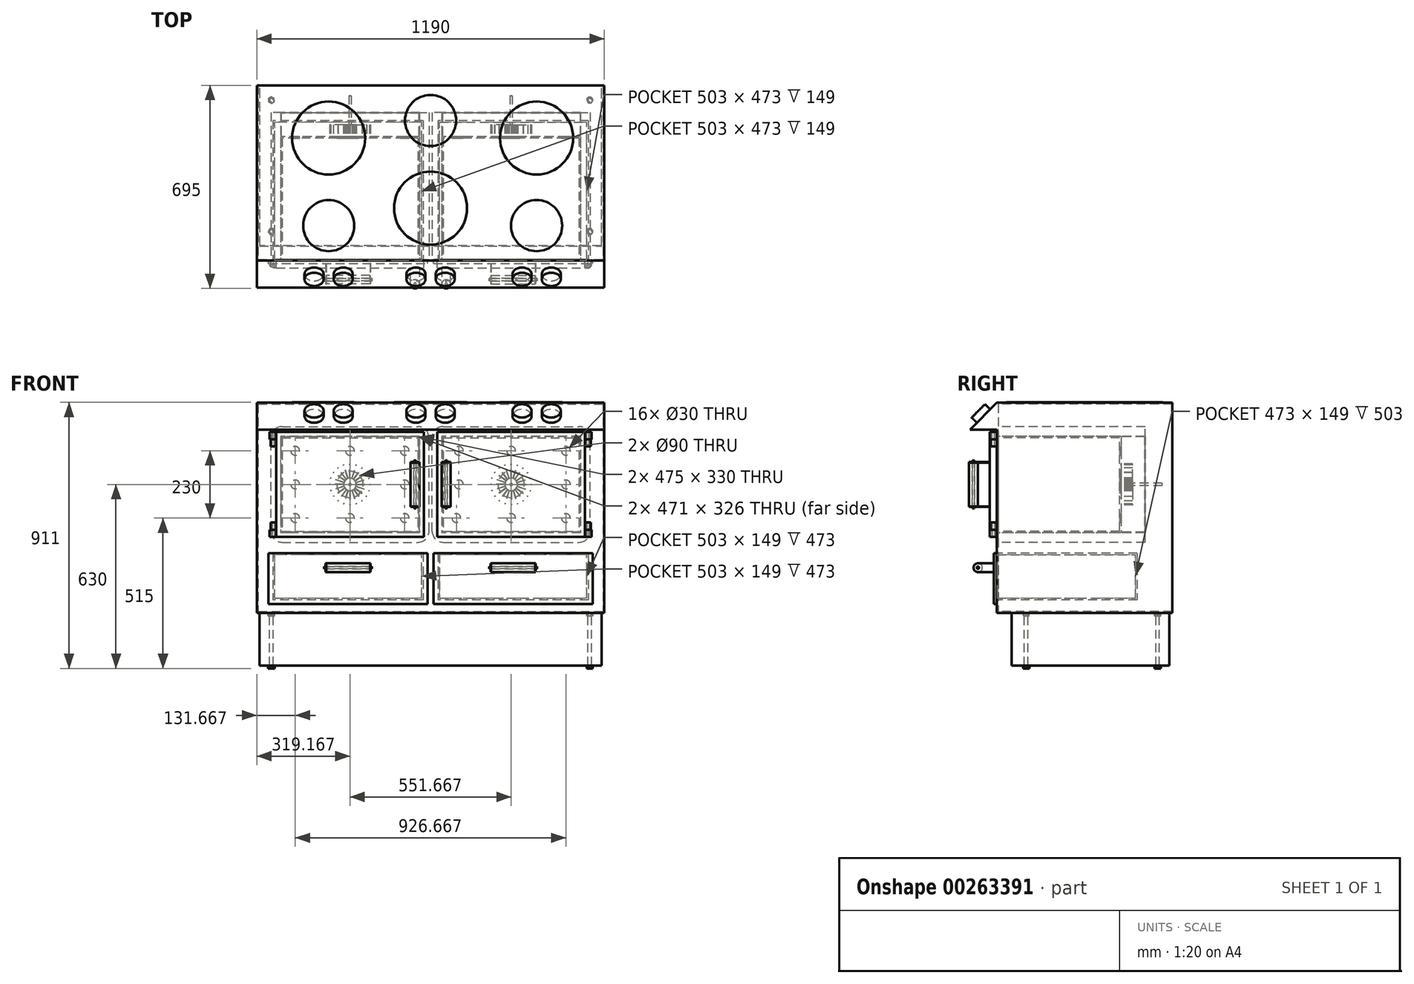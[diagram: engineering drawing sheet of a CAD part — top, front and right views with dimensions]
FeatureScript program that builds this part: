
annotation { "Feature Type Name" : "Feature", "Feature Type Description" : "" }
export const myFeature = defineFeature(function(context is Context, id is Id, definition is map)
    precondition{}
    {
        {
            assignVariable(context, id + "F0", {"name" : "Height", "anyValue" : 910});
        }
        {
            assignVariable(context, id + "F1", {"name" : "Thickness", "anyValue" : 5});
        }
        {
            assignVariable(context, id + "F2", {"name" : "OvenDepth", "anyValue" : 420});
        }
        {
            assignVariable(context, id + "F3", {"name" : "ToeHeight", "anyValue" : 190});
        }
        {
            var Q0;
            Q0=qCreatedBy(makeId("Top.planeOp"),FACE);
            cPlane(context, id + "F4", {"entities" : qUnion([Q0]), "cplaneType" : CPlaneType.OFFSET, "offset" : (getVariable(context, 'ToeHeight')) * mm, "width" : 150 * mm, "height" : 150 * mm});
        }
        {
            var Q0;
            Q0=qCreatedBy(id+"F4.planeOp",FACE);
            var sketch = newSketch(context, id + "F5", { "sketchPlane" : qUnion([Q0])});
            skLineSegment(sketch, "E0.bottom", {"start": v(0, 0) * mm, "end": v(1190, 0) * mm});
            skLineSegment(sketch, "E0.top", {"start": v(0, -600) * mm, "end": v(1190, -600) * mm});
            skLineSegment(sketch, "E0.left", {"start": v(0, 0) * mm, "end": v(0, -600) * mm});
            skLineSegment(sketch, "E0.right", {"start": v(1190, 0) * mm, "end": v(1190, -600) * mm});
            skSolve(sketch);
        }
        {
            var Q0;
            Q0 = qSketchRegion(id + "F5", true);
            extrude(context, id + "F6", {"entities" : qUnion([Q0]), "depth" : (getVariable(context, 'Height') - getVariable(context, 'ToeHeight')) * mm});
        }
        {
            var Q0;
            Q0=makeQuery(id+"F6.opExtrude","SWEPT_FACE",FACE,{"disambiguationData":[OSD([sQuery(id+"F5.wireOp",EDGE,"E0.bottom")])]});
            var Q1;
            Q1=makeQuery(id+"F6.opExtrude","SWEPT_BODY",BODY,{"disambiguationData":[OSD([sQuery(id+"F5.wireOp",EDGE,"E0.bottom"),sQuery(id+"F5.wireOp",EDGE,"E0.top"),sQuery(id+"F5.wireOp",EDGE,"E0.left"),sQuery(id+"F5.wireOp",EDGE,"E0.right")])]});
            shell(context, id + "F7", {"entities" : qUnion([Q0]), "parts" : qUnion([Q1]), "thickness" : (getVariable(context, 'Thickness')) * mm});
        }
        {
            var Q0;
            Q0=makeQuery(id+"F6.opExtrude","SWEPT_FACE",FACE,{"disambiguationData":[OSD([sQuery(id+"F5.wireOp",EDGE,"E0.top")])]});
            var sketch = newSketch(context, id + "F8", { "sketchPlane" : qUnion([Q0])});
            skLineSegment(sketch, "E1.bottom", {"start": v(638.33, 790) * mm, "end": v(1103.33, 790) * mm});
            skLineSegment(sketch, "E1.top", {"start": v(638.33, 470) * mm, "end": v(1103.33, 470) * mm});
            skLineSegment(sketch, "E1.left", {"start": v(638.33, 790) * mm, "end": v(638.33, 470) * mm});
            skLineSegment(sketch, "E1.right", {"start": v(1103.33, 790) * mm, "end": v(1103.33, 470) * mm});
            skLineSegment(sketch, "E2.bottom", {"start": v(86.67, 790) * mm, "end": v(551.67, 790) * mm});
            skLineSegment(sketch, "E2.top", {"start": v(86.67, 470) * mm, "end": v(551.67, 470) * mm});
            skLineSegment(sketch, "E2.left", {"start": v(86.67, 790) * mm, "end": v(86.67, 470) * mm});
            skLineSegment(sketch, "E2.right", {"start": v(551.67, 790) * mm, "end": v(551.67, 470) * mm});
            skLineSegment(sketch, "E3", {"start": v(0, 550) * mm, "end": v(86.67, 550) * mm, "construction": true});
            skLineSegment(sketch, "E4", {"start": v(551.67, 550) * mm, "end": v(638.33, 550) * mm, "construction": true});
            skLineSegment(sketch, "E5", {"start": v(1103.33, 550) * mm, "end": v(1190, 550) * mm, "construction": true});
            skSolve(sketch);
        }
        {
            var Q0;
            Q0 = qSketchRegion(id + "F8", true);
            extrude(context, id + "F9", {"entities" : qUnion([Q0]), "operationType" : NewBodyOperationType.REMOVE, "oppositeDirection" : true, "depth" : 25 * mm});
        }
        {
            var Q0;
            Q0=makeQuery(id+"F7.opShell","OFFSET_FACE",FACE,{"disambiguationData":[OSD([sQuery(id+"F5.wireOp",EDGE,"E0.top")])]});
            var sketch = newSketch(context, id + "F10", { "sketchPlane" : qUnion([Q0])});
            skLineSegment(sketch, "E6.0", {"start": v(-1103.33, 790) * mm, "end": v(-638.33, 790) * mm});
            skLineSegment(sketch, "E7.0", {"start": v(-1103.33, 470) * mm, "end": v(-1103.33, 790) * mm});
            skLineSegment(sketch, "E8.0", {"start": v(-1103.33, 470) * mm, "end": v(-638.33, 470) * mm});
            skLineSegment(sketch, "E9.0", {"start": v(-638.33, 470) * mm, "end": v(-638.33, 790) * mm});
            skLineSegment(sketch, "E10.0", {"start": v(-551.67, 470) * mm, "end": v(-551.67, 790) * mm});
            skLineSegment(sketch, "E11.0", {"start": v(-551.67, 790) * mm, "end": v(-86.67, 790) * mm});
            skLineSegment(sketch, "E12.0", {"start": v(-86.67, 470) * mm, "end": v(-86.67, 790) * mm});
            skLineSegment(sketch, "E13.0", {"start": v(-551.67, 470) * mm, "end": v(-86.67, 470) * mm});
            skLineSegment(sketch, "E14.bottom", {"start": v(-1108.33, 795) * mm, "end": v(-633.33, 795) * mm});
            skLineSegment(sketch, "E14.top", {"start": v(-1108.33, 465) * mm, "end": v(-633.33, 465) * mm});
            skLineSegment(sketch, "E14.left", {"start": v(-1108.33, 795) * mm, "end": v(-1108.33, 465) * mm});
            skLineSegment(sketch, "E14.right", {"start": v(-633.33, 795) * mm, "end": v(-633.33, 465) * mm});
            skLineSegment(sketch, "E15.bottom", {"start": v(-556.67, 795) * mm, "end": v(-81.67, 795) * mm});
            skLineSegment(sketch, "E15.top", {"start": v(-556.67, 465) * mm, "end": v(-81.67, 465) * mm});
            skLineSegment(sketch, "E15.left", {"start": v(-556.67, 795) * mm, "end": v(-556.67, 465) * mm});
            skLineSegment(sketch, "E15.right", {"start": v(-81.67, 795) * mm, "end": v(-81.67, 465) * mm});
            skSolve(sketch);
        }
        {
            var Q0;
            Q0 = qSketchRegion(id + "F10", true);
            extrude(context, id + "F11", {"entities" : qUnion([Q0]), "operationType" : NewBodyOperationType.ADD, "depth" : (getVariable(context, 'OvenDepth') - getVariable(context, 'Thickness')) * mm});
        }
        {
            var Q0;
            Q0=makeQuery(id+"F11.opExtrude","CAP_FACE",FACE,{"disambiguationData":[OSD([sQuery(id+"F10.wireOp",EDGE,"E6.0"),sQuery(id+"F10.wireOp",EDGE,"E7.0"),sQuery(id+"F10.wireOp",EDGE,"E8.0"),sQuery(id+"F10.wireOp",EDGE,"E9.0"),sQuery(id+"F10.wireOp",EDGE,"E14.bottom"),sQuery(id+"F10.wireOp",EDGE,"E14.top"),sQuery(id+"F10.wireOp",EDGE,"E14.left"),sQuery(id+"F10.wireOp",EDGE,"E14.right")])],"isStart":false});
            var sketch = newSketch(context, id + "F12", { "sketchPlane" : qUnion([Q0])});
            skLineSegment(sketch, "E16.bottom", {"start": v(-1108.33, 795) * mm, "end": v(-633.33, 795) * mm});
            skLineSegment(sketch, "E16.top", {"start": v(-1108.33, 465) * mm, "end": v(-633.33, 465) * mm});
            skLineSegment(sketch, "E16.left", {"start": v(-1108.33, 795) * mm, "end": v(-1108.33, 465) * mm});
            skLineSegment(sketch, "E16.right", {"start": v(-633.33, 795) * mm, "end": v(-633.33, 465) * mm});
            skLineSegment(sketch, "E17.bottom", {"start": v(-556.67, 795) * mm, "end": v(-81.67, 795) * mm});
            skLineSegment(sketch, "E17.top", {"start": v(-556.67, 465) * mm, "end": v(-81.67, 465) * mm});
            skLineSegment(sketch, "E17.left", {"start": v(-556.67, 795) * mm, "end": v(-556.67, 465) * mm});
            skLineSegment(sketch, "E17.right", {"start": v(-81.67, 795) * mm, "end": v(-81.67, 465) * mm});
            skSolve(sketch);
        }
        {
            var Q0;
            Q0 = qSketchRegion(id + "F12", true);
            extrude(context, id + "F13", {"entities" : qUnion([Q0]), "operationType" : NewBodyOperationType.ADD, "depth" : (getVariable(context, 'Thickness')) * mm});
        }
        {
            var Q0;
            Q0=makeQuery(id+"F6.opExtrude","SWEPT_FACE",FACE,{"disambiguationData":[OSD([sQuery(id+"F5.wireOp",EDGE,"E0.top")])]});
            var sketch = newSketch(context, id + "F14", { "sketchPlane" : qUnion([Q0])});
            skLineSegment(sketch, "E18.bottom", {"start": v(60, 390) * mm, "end": v(565, 390) * mm});
            skLineSegment(sketch, "E18.top", {"start": v(60, 240) * mm, "end": v(565, 240) * mm});
            skLineSegment(sketch, "E18.left", {"start": v(60, 390) * mm, "end": v(60, 240) * mm});
            skLineSegment(sketch, "E18.right", {"start": v(565, 390) * mm, "end": v(565, 240) * mm});
            skLineSegment(sketch, "E19.bottom", {"start": v(625, 390) * mm, "end": v(1130, 390) * mm});
            skLineSegment(sketch, "E19.top", {"start": v(625, 240) * mm, "end": v(1130, 240) * mm});
            skLineSegment(sketch, "E19.left", {"start": v(625, 390) * mm, "end": v(625, 240) * mm});
            skLineSegment(sketch, "E19.right", {"start": v(1130, 390) * mm, "end": v(1130, 240) * mm});
            skLineSegment(sketch, "E20", {"start": v(0, 306.12) * mm, "end": v(60, 306.12) * mm, "construction": true});
            skLineSegment(sketch, "E21", {"start": v(565, 306.12) * mm, "end": v(625, 306.12) * mm, "construction": true});
            skLineSegment(sketch, "E22", {"start": v(1130, 306.12) * mm, "end": v(1190, 306.12) * mm, "construction": true});
            skPoint(sketch, "E22.startSnap0", {"position": v(1130, 315) * mm});
            skLineSegment(sketch, "E23", {"start": v(293.85, 470) * mm, "end": v(293.85, 390) * mm, "construction": true});
            skLineSegment(sketch, "E24", {"start": v(312.5, 240) * mm, "end": v(312.5, 160) * mm, "construction": true});
            skSolve(sketch);
        }
        {
            var Q0;
            Q0 = qSketchRegion(id + "F14", true);
            extrude(context, id + "F15", {"entities" : qUnion([Q0]), "operationType" : NewBodyOperationType.REMOVE, "oppositeDirection" : true, "depth" : 25 * mm});
        }
        {
            var Q0;
            Q0=makeQuery(id+"F7.opShell","OFFSET_FACE",FACE,{"disambiguationData":[OSD([sQuery(id+"F5.wireOp",EDGE,"E0.top")])]});
            var sketch = newSketch(context, id + "F16", { "sketchPlane" : qUnion([Q0])});
            skLineSegment(sketch, "E25.0", {"start": v(-1130, 240) * mm, "end": v(-625, 240) * mm});
            skLineSegment(sketch, "E26.0", {"start": v(-1130, 390) * mm, "end": v(-625, 390) * mm});
            skLineSegment(sketch, "E27.0", {"start": v(-1130, 240) * mm, "end": v(-1130, 390) * mm});
            skLineSegment(sketch, "E28.0", {"start": v(-625, 240) * mm, "end": v(-625, 390) * mm});
            skLineSegment(sketch, "E29.0", {"start": v(-565, 240) * mm, "end": v(-565, 390) * mm});
            skLineSegment(sketch, "E30.0", {"start": v(-565, 390) * mm, "end": v(-60, 390) * mm});
            skLineSegment(sketch, "E31.0", {"start": v(-60, 240) * mm, "end": v(-60, 390) * mm});
            skLineSegment(sketch, "E32.0", {"start": v(-565, 240) * mm, "end": v(-60, 240) * mm});
            skLineSegment(sketch, "E33.bottom", {"start": v(-1135, 395) * mm, "end": v(-620, 395) * mm});
            skLineSegment(sketch, "E33.top", {"start": v(-1135, 235) * mm, "end": v(-620, 235) * mm});
            skLineSegment(sketch, "E33.left", {"start": v(-1135, 395) * mm, "end": v(-1135, 235) * mm});
            skLineSegment(sketch, "E33.right", {"start": v(-620, 395) * mm, "end": v(-620, 235) * mm});
            skLineSegment(sketch, "E34.bottom", {"start": v(-570, 395) * mm, "end": v(-55, 395) * mm});
            skLineSegment(sketch, "E34.top", {"start": v(-570, 235) * mm, "end": v(-55, 235) * mm});
            skLineSegment(sketch, "E34.left", {"start": v(-570, 395) * mm, "end": v(-570, 235) * mm});
            skLineSegment(sketch, "E34.right", {"start": v(-55, 395) * mm, "end": v(-55, 235) * mm});
            skSolve(sketch);
        }
        {
            var Q0;
            Q0 = qSketchRegion(id + "F16", true);
            extrude(context, id + "F17", {"entities" : qUnion([Q0]), "operationType" : NewBodyOperationType.ADD, "depth" : (getVariable(context, 'OvenDepth') + 50) * mm});
        }
        {
            var Q0;
            Q0=makeQuery(id+"F17.opExtrude","CAP_FACE",FACE,{"disambiguationData":[OSD([sQuery(id+"F16.wireOp",EDGE,"E25.0"),sQuery(id+"F16.wireOp",EDGE,"E26.0"),sQuery(id+"F16.wireOp",EDGE,"E27.0"),sQuery(id+"F16.wireOp",EDGE,"E28.0"),sQuery(id+"F16.wireOp",EDGE,"E33.bottom"),sQuery(id+"F16.wireOp",EDGE,"E33.top"),sQuery(id+"F16.wireOp",EDGE,"E33.left"),sQuery(id+"F16.wireOp",EDGE,"E33.right")])],"isStart":false});
            var sketch = newSketch(context, id + "F18", { "sketchPlane" : qUnion([Q0])});
            skLineSegment(sketch, "E35.bottom", {"start": v(-1135, 395) * mm, "end": v(-620, 395) * mm});
            skLineSegment(sketch, "E35.top", {"start": v(-1135, 235) * mm, "end": v(-620, 235) * mm});
            skLineSegment(sketch, "E35.left", {"start": v(-1135, 395) * mm, "end": v(-1135, 235) * mm});
            skLineSegment(sketch, "E35.right", {"start": v(-620, 395) * mm, "end": v(-620, 235) * mm});
            skLineSegment(sketch, "E36.bottom", {"start": v(-570, 395) * mm, "end": v(-55, 395) * mm});
            skLineSegment(sketch, "E36.top", {"start": v(-570, 235) * mm, "end": v(-55, 235) * mm});
            skLineSegment(sketch, "E36.left", {"start": v(-570, 395) * mm, "end": v(-570, 235) * mm});
            skLineSegment(sketch, "E36.right", {"start": v(-55, 395) * mm, "end": v(-55, 235) * mm});
            skSolve(sketch);
        }
        {
            var Q0;
            Q0 = qSketchRegion(id + "F18", true);
            extrude(context, id + "F19", {"entities" : qUnion([Q0]), "operationType" : NewBodyOperationType.ADD, "depth" : (getVariable(context, 'Thickness')) * mm});
        }
        {
            var Q0;
            Q0=makeQuery(id+"F6.opExtrude","CAP_FACE",FACE,{"disambiguationData":[OSD([sQuery(id+"F5.wireOp",EDGE,"E0.bottom"),sQuery(id+"F5.wireOp",EDGE,"E0.top"),sQuery(id+"F5.wireOp",EDGE,"E0.left"),sQuery(id+"F5.wireOp",EDGE,"E0.right")])],"isStart":true});
            var sketch = newSketch(context, id + "F20", { "sketchPlane" : qUnion([Q0])});
            skCircle(sketch, "E37.cCircle", {"center": v(50, 500) * mm, "radius": 9.5 * mm, "construction": true});
            skLineSegment(sketch, "E37.0", {"start": v(55.48, 490.5) * mm, "end": v(44.52, 490.5) * mm});
            skLineSegment(sketch, "E37.1", {"start": v(44.52, 490.5) * mm, "end": v(39.03, 500) * mm});
            skLineSegment(sketch, "E37.2", {"start": v(39.03, 500) * mm, "end": v(44.52, 509.5) * mm});
            skLineSegment(sketch, "E37.3", {"start": v(44.52, 509.5) * mm, "end": v(55.48, 509.5) * mm});
            skLineSegment(sketch, "E37.4", {"start": v(55.48, 509.5) * mm, "end": v(60.97, 500) * mm});
            skLineSegment(sketch, "E37.5", {"start": v(60.97, 500) * mm, "end": v(55.48, 490.5) * mm});
            skPoint(sketch, "E37.0.midPoint", {"position": v(50, 490.5) * mm});
            skCircle(sketch, "E38.cCircle", {"center": v(1140, 500) * mm, "radius": 9.5 * mm, "construction": true});
            skLineSegment(sketch, "E38.0", {"start": v(1145.48, 490.5) * mm, "end": v(1134.52, 490.5) * mm});
            skLineSegment(sketch, "E38.1", {"start": v(1134.52, 490.5) * mm, "end": v(1129.03, 500) * mm});
            skLineSegment(sketch, "E38.2", {"start": v(1129.03, 500) * mm, "end": v(1134.52, 509.5) * mm});
            skLineSegment(sketch, "E38.3", {"start": v(1134.52, 509.5) * mm, "end": v(1145.48, 509.5) * mm});
            skLineSegment(sketch, "E38.4", {"start": v(1145.48, 509.5) * mm, "end": v(1150.97, 500) * mm});
            skLineSegment(sketch, "E38.5", {"start": v(1150.97, 500) * mm, "end": v(1145.48, 490.5) * mm});
            skPoint(sketch, "E38.0.midPoint", {"position": v(1140, 490.5) * mm});
            skCircle(sketch, "E39.cCircle", {"center": v(1140, 50) * mm, "radius": 9.5 * mm, "construction": true});
            skLineSegment(sketch, "E39.0", {"start": v(1150.97, 50) * mm, "end": v(1145.48, 40.5) * mm});
            skLineSegment(sketch, "E39.1", {"start": v(1145.48, 40.5) * mm, "end": v(1134.52, 40.5) * mm});
            skLineSegment(sketch, "E39.2", {"start": v(1134.52, 40.5) * mm, "end": v(1129.03, 50) * mm});
            skLineSegment(sketch, "E39.3", {"start": v(1129.03, 50) * mm, "end": v(1134.52, 59.5) * mm});
            skLineSegment(sketch, "E39.4", {"start": v(1134.52, 59.5) * mm, "end": v(1145.48, 59.5) * mm});
            skLineSegment(sketch, "E39.5", {"start": v(1145.48, 59.5) * mm, "end": v(1150.97, 50) * mm});
            skPoint(sketch, "E39.0.midPoint", {"position": v(1148.23, 45.25) * mm});
            skCircle(sketch, "E40.cCircle", {"center": v(50, 50) * mm, "radius": 9.5 * mm, "construction": true});
            skLineSegment(sketch, "E40.0", {"start": v(49, 39.08) * mm, "end": v(40.04, 45.4) * mm});
            skLineSegment(sketch, "E40.1", {"start": v(40.04, 45.4) * mm, "end": v(41.04, 56.33) * mm});
            skLineSegment(sketch, "E40.2", {"start": v(41.04, 56.33) * mm, "end": v(51, 60.92) * mm});
            skLineSegment(sketch, "E40.3", {"start": v(51, 60.92) * mm, "end": v(59.96, 54.6) * mm});
            skLineSegment(sketch, "E40.4", {"start": v(59.96, 54.6) * mm, "end": v(58.96, 43.67) * mm});
            skLineSegment(sketch, "E40.5", {"start": v(58.96, 43.67) * mm, "end": v(49, 39.08) * mm});
            skPoint(sketch, "E40.0.midPoint", {"position": v(44.52, 42.24) * mm});
            skCircle(sketch, "E41", {"center": v(50, 500) * mm, "radius": 6 * mm});
            skCircle(sketch, "E42", {"center": v(50, 50) * mm, "radius": 6 * mm});
            skCircle(sketch, "E43", {"center": v(1140, 50) * mm, "radius": 6 * mm});
            skCircle(sketch, "E44", {"center": v(1140, 500) * mm, "radius": 6 * mm});
            skSolve(sketch);
        }
        {
            var Q0;
            Q0 = qSketchRegion(id + "F20", true);
            extrude(context, id + "F21", {"entities" : qUnion([Q0]), "depth" : 10 * mm});
        }
        {
            var Q0;
            Q0=makeQuery(id+"F6.opExtrude","CAP_FACE",FACE,{"disambiguationData":[OSD([sQuery(id+"F5.wireOp",EDGE,"E0.bottom"),sQuery(id+"F5.wireOp",EDGE,"E0.top"),sQuery(id+"F5.wireOp",EDGE,"E0.left"),sQuery(id+"F5.wireOp",EDGE,"E0.right")])],"isStart":true});
            var sketch = newSketch(context, id + "F22", { "sketchPlane" : qUnion([Q0])});
            skCircle(sketch, "E45.0", {"center": v(50, 500) * mm, "radius": 6 * mm});
            skCircle(sketch, "E46.0", {"center": v(50, 50) * mm, "radius": 6 * mm});
            skCircle(sketch, "E47.0", {"center": v(1140, 50) * mm, "radius": 6 * mm});
            skCircle(sketch, "E48.0", {"center": v(1140, 500) * mm, "radius": 6 * mm});
            skSolve(sketch);
        }
        {
            var Q0;
            Q0 = qSketchRegion(id + "F22", true);
            extrude(context, id + "F23", {"entities" : qUnion([Q0]), "depth" : (getVariable(context, 'ToeHeight') - 10) * mm});
        }
        {
            var Q0;
            Q0=makeQuery(id+"F23.opExtrude","CAP_FACE",FACE,{"disambiguationData":[OSD([sQuery(id+"F22.wireOp",EDGE,"E48.0")])],"isStart":false});
            var sketch = newSketch(context, id + "F24", { "sketchPlane" : qUnion([Q0])});
            skCircle(sketch, "E49.cCircle", {"center": v(1140, 500) * mm, "radius": 9.5 * mm, "construction": true});
            skLineSegment(sketch, "E49.0", {"start": v(1150.28, 496.17) * mm, "end": v(1141.82, 489.18) * mm});
            skLineSegment(sketch, "E49.1", {"start": v(1141.82, 489.18) * mm, "end": v(1131.54, 493.01) * mm});
            skLineSegment(sketch, "E49.2", {"start": v(1131.54, 493.01) * mm, "end": v(1129.72, 503.83) * mm});
            skLineSegment(sketch, "E49.3", {"start": v(1129.72, 503.83) * mm, "end": v(1138.18, 510.82) * mm});
            skLineSegment(sketch, "E49.4", {"start": v(1138.18, 510.82) * mm, "end": v(1148.46, 506.99) * mm});
            skLineSegment(sketch, "E49.5", {"start": v(1148.46, 506.99) * mm, "end": v(1150.28, 496.17) * mm});
            skPoint(sketch, "E49.0.midPoint", {"position": v(1146.05, 492.68) * mm});
            skCircle(sketch, "E50.cCircle", {"center": v(1140, 50) * mm, "radius": 9.5 * mm, "construction": true});
            skLineSegment(sketch, "E50.0", {"start": v(1141.82, 60.82) * mm, "end": v(1150.28, 53.83) * mm});
            skLineSegment(sketch, "E50.1", {"start": v(1150.28, 53.83) * mm, "end": v(1148.46, 43.01) * mm});
            skLineSegment(sketch, "E50.2", {"start": v(1148.46, 43.01) * mm, "end": v(1138.18, 39.18) * mm});
            skLineSegment(sketch, "E50.3", {"start": v(1138.18, 39.18) * mm, "end": v(1129.72, 46.17) * mm});
            skLineSegment(sketch, "E50.4", {"start": v(1129.72, 46.17) * mm, "end": v(1131.54, 56.99) * mm});
            skLineSegment(sketch, "E50.5", {"start": v(1131.54, 56.99) * mm, "end": v(1141.82, 60.82) * mm});
            skPoint(sketch, "E50.0.midPoint", {"position": v(1146.05, 57.32) * mm});
            skCircle(sketch, "E51.cCircle", {"center": v(50, 50) * mm, "radius": 9.5 * mm, "construction": true});
            skLineSegment(sketch, "E51.0", {"start": v(59.5, 55.48) * mm, "end": v(59.5, 44.52) * mm});
            skLineSegment(sketch, "E51.1", {"start": v(59.5, 44.52) * mm, "end": v(50, 39.03) * mm});
            skLineSegment(sketch, "E51.2", {"start": v(50, 39.03) * mm, "end": v(40.5, 44.52) * mm});
            skLineSegment(sketch, "E51.3", {"start": v(40.5, 44.52) * mm, "end": v(40.5, 55.48) * mm});
            skLineSegment(sketch, "E51.4", {"start": v(40.5, 55.48) * mm, "end": v(50, 60.97) * mm});
            skLineSegment(sketch, "E51.5", {"start": v(50, 60.97) * mm, "end": v(59.5, 55.48) * mm});
            skPoint(sketch, "E51.0.midPoint", {"position": v(59.5, 50) * mm});
            skCircle(sketch, "E52.cCircle", {"center": v(50, 500) * mm, "radius": 9.5 * mm, "construction": true});
            skLineSegment(sketch, "E52.0", {"start": v(55.48, 490.5) * mm, "end": v(44.52, 490.5) * mm});
            skLineSegment(sketch, "E52.1", {"start": v(44.52, 490.5) * mm, "end": v(39.03, 500) * mm});
            skLineSegment(sketch, "E52.2", {"start": v(39.03, 500) * mm, "end": v(44.52, 509.5) * mm});
            skLineSegment(sketch, "E52.3", {"start": v(44.52, 509.5) * mm, "end": v(55.48, 509.5) * mm});
            skLineSegment(sketch, "E52.4", {"start": v(55.48, 509.5) * mm, "end": v(60.97, 500) * mm});
            skLineSegment(sketch, "E52.5", {"start": v(60.97, 500) * mm, "end": v(55.48, 490.5) * mm});
            skPoint(sketch, "E52.0.midPoint", {"position": v(50, 490.5) * mm});
            skSolve(sketch);
        }
        {
            var Q0;
            Q0 = qSketchRegion(id + "F24", true);
            extrude(context, id + "F25", {"entities" : qUnion([Q0]), "operationType" : NewBodyOperationType.ADD, "depth" : 10 * mm});
        }
        {
            var Q0;
            Q0=makeQuery(id+"F6.opExtrude","CAP_FACE",FACE,{"disambiguationData":[OSD([sQuery(id+"F5.wireOp",EDGE,"E0.bottom"),sQuery(id+"F5.wireOp",EDGE,"E0.top"),sQuery(id+"F5.wireOp",EDGE,"E0.left"),sQuery(id+"F5.wireOp",EDGE,"E0.right")])],"isStart":true});
            var sketch = newSketch(context, id + "F26", { "sketchPlane" : qUnion([Q0])});
            skLineSegment(sketch, "E53", {"start": v(10, 10) * mm, "end": v(10, 550) * mm});
            skLineSegment(sketch, "E54", {"start": v(10, 550) * mm, "end": v(1180, 550) * mm});
            skLineSegment(sketch, "E55", {"start": v(1180, 550) * mm, "end": v(1180, 10) * mm});
            skLineSegment(sketch, "E56", {"start": v(1180, 10) * mm, "end": v(1179, 10) * mm});
            skLineSegment(sketch, "E57", {"start": v(1179, 10) * mm, "end": v(1179, 549) * mm});
            skLineSegment(sketch, "E58", {"start": v(1179, 549) * mm, "end": v(11, 549) * mm});
            skLineSegment(sketch, "E59", {"start": v(11, 549) * mm, "end": v(11, 10) * mm});
            skLineSegment(sketch, "E60", {"start": v(11, 10) * mm, "end": v(10, 10) * mm});
            skSolve(sketch);
        }
        {
            var Q0;
            Q0 = qSketchRegion(id + "F26", true);
            extrude(context, id + "F27", {"entities" : qUnion([Q0]), "depth" : (getVariable(context, 'ToeHeight') - 10) * mm});
        }
        {
            var Q0;
            Q0=makeQuery(id+"F19.opExtrude","CAP_FACE",FACE,{"disambiguationData":[OSD([sQuery(id+"F18.wireOp",EDGE,"E36.bottom"),sQuery(id+"F18.wireOp",EDGE,"E36.top"),sQuery(id+"F18.wireOp",EDGE,"E36.left"),sQuery(id+"F18.wireOp",EDGE,"E36.right")])],"isStart":true});
            var sketch = newSketch(context, id + "F28", { "sketchPlane" : qUnion([Q0])});
            skLineSegment(sketch, "E61.0.0", {"start": v(60, 390) * mm, "end": v(60, 240) * mm});
            skLineSegment(sketch, "E61.0.1", {"start": v(60, 240) * mm, "end": v(565, 240) * mm});
            skLineSegment(sketch, "E61.0.2", {"start": v(565, 240) * mm, "end": v(565, 390) * mm});
            skLineSegment(sketch, "E61.0.3", {"start": v(565, 390) * mm, "end": v(60, 390) * mm});
            skLineSegment(sketch, "E62.0.0", {"start": v(625, 390) * mm, "end": v(625, 240) * mm});
            skLineSegment(sketch, "E62.0.1", {"start": v(625, 240) * mm, "end": v(1130, 240) * mm});
            skLineSegment(sketch, "E62.0.2", {"start": v(1130, 240) * mm, "end": v(1130, 390) * mm});
            skLineSegment(sketch, "E62.0.3", {"start": v(1130, 390) * mm, "end": v(625, 390) * mm});
            skSolve(sketch);
        }
        {
            var Q0;
            Q0 = qSketchRegion(id + "F28", true);
            var Q1;
            Q1=makeQuery(id+"F6.opExtrude","SWEPT_FACE",FACE,{"disambiguationData":[OSD([sQuery(id+"F5.wireOp",EDGE,"E0.top")])]});
            extrude(context, id + "F29", {"entities" : qUnion([Q0]), "endBound" : BoundingType.UP_TO_SURFACE, "endBoundEntityFace" : qUnion([Q1]), "depth" : 25 * mm});
        }
        {
            var Q0;
            Q0=makeQuery(id+"F29.opExtrude","SWEPT_FACE",FACE,{"disambiguationData":[OSD([sQuery(id+"F28.wireOp",EDGE,"E61.0.3")])]});
            var Q1;
            Q1=makeQuery(id+"F29.opExtrude","SWEPT_FACE",FACE,{"disambiguationData":[OSD([sQuery(id+"F28.wireOp",EDGE,"E62.0.3")])]});
            shell(context, id + "F30", {"entities" : qUnion([Q0, Q1]), "thickness" : 1 * mm});
        }
        {
            var Q0;
            Q0=makeQuery(id+"F6.opExtrude","SWEPT_FACE",FACE,{"disambiguationData":[OSD([sQuery(id+"F5.wireOp",EDGE,"E0.top")])]});
            var sketch = newSketch(context, id + "F31", { "sketchPlane" : qUnion([Q0])});
            skLineSegment(sketch, "E63.bottom", {"start": v(40, 395) * mm, "end": v(585, 395) * mm});
            skLineSegment(sketch, "E63.top", {"start": v(40, 220) * mm, "end": v(585, 220) * mm});
            skLineSegment(sketch, "E63.left", {"start": v(40, 395) * mm, "end": v(40, 220) * mm});
            skLineSegment(sketch, "E63.right", {"start": v(585, 395) * mm, "end": v(585, 220) * mm});
            skLineSegment(sketch, "E64.bottom", {"start": v(605, 395) * mm, "end": v(1150, 395) * mm});
            skLineSegment(sketch, "E64.top", {"start": v(605, 220) * mm, "end": v(1150, 220) * mm});
            skLineSegment(sketch, "E64.left", {"start": v(605, 395) * mm, "end": v(605, 220) * mm});
            skLineSegment(sketch, "E64.right", {"start": v(1150, 395) * mm, "end": v(1150, 220) * mm});
            skSolve(sketch);
        }
        {
            var Q0;
            Q0 = qSketchRegion(id + "F31", true);
            extrude(context, id + "F32", {"entities" : qUnion([Q0]), "operationType" : NewBodyOperationType.ADD, "depth" : 10 * mm});
        }
        {
            var Q0;
            Q0=makeQuery(id+"F6.opExtrude","SWEPT_FACE",FACE,{"disambiguationData":[OSD([sQuery(id+"F5.wireOp",EDGE,"E0.top")])]});
            var sketch = newSketch(context, id + "F33", { "sketchPlane" : qUnion([Q0])});
            skLineSegment(sketch, "E65.bottom", {"start": v(66.67, 810) * mm, "end": v(571.67, 810) * mm});
            skLineSegment(sketch, "E65.top", {"start": v(66.67, 450) * mm, "end": v(571.67, 450) * mm});
            skLineSegment(sketch, "E65.left", {"start": v(66.67, 810) * mm, "end": v(66.67, 450) * mm});
            skLineSegment(sketch, "E65.right", {"start": v(571.67, 810) * mm, "end": v(571.67, 450) * mm});
            skLineSegment(sketch, "E66.bottom", {"start": v(618.33, 810) * mm, "end": v(1123.33, 810) * mm});
            skLineSegment(sketch, "E66.top", {"start": v(618.33, 450) * mm, "end": v(1123.33, 450) * mm});
            skLineSegment(sketch, "E66.left", {"start": v(618.33, 810) * mm, "end": v(618.33, 450) * mm});
            skLineSegment(sketch, "E66.right", {"start": v(1123.33, 810) * mm, "end": v(1123.33, 450) * mm});
            skSolve(sketch);
        }
        {
            var Q0;
            Q0 = qSketchRegion(id + "F33", true);
            extrude(context, id + "F34", {"entities" : qUnion([Q0]), "depth" : 25 * mm});
        }
        {
            var Q0;
            Q0=makeQuery(id+"F6.opExtrude","SWEPT_FACE",FACE,{"disambiguationData":[OSD([sQuery(id+"F5.wireOp",EDGE,"E0.left")])]});
            var sketch = newSketch(context, id + "F35", { "sketchPlane" : qUnion([Q0])});
            skLineSegment(sketch, "E67", {"start": v(600, 910) * mm, "end": v(691.92, 818.08) * mm});
            skLineSegment(sketch, "E68", {"start": v(691.92, 818.08) * mm, "end": v(600, 818.08) * mm});
            skLineSegment(sketch, "E69", {"start": v(600, 818.08) * mm, "end": v(600, 910) * mm});
            skSolve(sketch);
        }
        {
            var Q0;
            Q0 = qSketchRegion(id + "F35", true);
            var Q1;
            Q1=makeQuery(id+"F6.opExtrude","SWEPT_FACE",FACE,{"disambiguationData":[OSD([sQuery(id+"F5.wireOp",EDGE,"E0.right")])]});
            extrude(context, id + "F36", {"entities" : qUnion([Q0]), "operationType" : NewBodyOperationType.ADD, "endBound" : BoundingType.UP_TO_SURFACE, "oppositeDirection" : true, "endBoundEntityFace" : qUnion([Q1]), "depth" : 25 * mm});
        }
        {
            var Q0;
            Q0=makeQuery(id+"F6.opExtrude","CAP_FACE",FACE,{"disambiguationData":[OSD([sQuery(id+"F5.wireOp",EDGE,"E0.bottom"),sQuery(id+"F5.wireOp",EDGE,"E0.top"),sQuery(id+"F5.wireOp",EDGE,"E0.left"),sQuery(id+"F5.wireOp",EDGE,"E0.right")])],"isStart":false});
            var sketch = newSketch(context, id + "F37", { "sketchPlane" : qUnion([Q0])});
            skCircle(sketch, "E70", {"center": v(246.22, -480) * mm, "radius": 87.5 * mm});
            skCircle(sketch, "E71", {"center": v(246.22, -180) * mm, "radius": 125 * mm});
            skCircle(sketch, "E72", {"center": v(595, -420) * mm, "radius": 125 * mm});
            skCircle(sketch, "E73", {"center": v(595, -120) * mm, "radius": 87.5 * mm});
            skCircle(sketch, "E74", {"center": v(958.01, -180) * mm, "radius": 125 * mm});
            skCircle(sketch, "E75", {"center": v(958.01, -480) * mm, "radius": 87.5 * mm});
            skLineSegment(sketch, "E76", {"start": v(595, 0) * mm, "end": v(595, -600) * mm, "construction": true});
            skLineSegment(sketch, "E77", {"start": v(958.01, 52.1) * mm, "end": v(958.01, -836.9) * mm, "construction": true});
            skLineSegment(sketch, "E78", {"start": v(246.22, 125.1) * mm, "end": v(246.22, -765.52) * mm, "construction": true});
            skSolve(sketch);
        }
        {
            var Q0;
            Q0 = qSketchRegion(id + "F37", true);
            extrude(context, id + "F38", {"entities" : qUnion([Q0]), "depth" : 1 * mm});
        }
        {
            var Q0;
            Q0=makeQuery(id+"F34.opExtrude","SWEPT_FACE",FACE,{"disambiguationData":[OSD([sQuery(id+"F33.wireOp",EDGE,"E65.top")])]});
            var sketch = newSketch(context, id + "F39", { "sketchPlane" : qUnion([Q0])});
            skCircle(sketch, "E79", {"center": v(56.67, 612.5) * mm, "radius": 4 * mm});
            skLineSegment(sketch, "E80", {"start": v(66.67, 612.5) * mm, "end": v(16.3, 612.5) * mm, "construction": true});
            skLineSegment(sketch, "E81.0", {"start": v(66.67, 625) * mm, "end": v(66.67, 600) * mm});
            skLineSegment(sketch, "E82", {"start": v(66.67, 625) * mm, "end": v(56.67, 625) * mm});
            skLineSegment(sketch, "E83", {"start": v(66.67, 600) * mm, "end": v(56.67, 600) * mm});
            skArc(sketch, "E84", {"start": v(56.67, 625) * mm, "mid": v(44.17, 612.5) * mm, "end": v(56.67, 600) * mm});
            skSolve(sketch);
        }
        {
            var Q0;
            Q0 = qSketchRegion(id + "F39", true);
            extrude(context, id + "F40", {"entities" : qUnion([Q0]), "oppositeDirection" : true, "depth" : 25 * mm});
        }
        {
            var Q0;
            Q0=makeQuery(id+"F40.opExtrude","CAP_FACE",FACE,{"disambiguationData":[OSD([sQuery(id+"F39.wireOp",EDGE,"E79"),sQuery(id+"F39.wireOp",EDGE,"E81.0"),sQuery(id+"F39.wireOp",EDGE,"E82"),sQuery(id+"F39.wireOp",EDGE,"E83"),sQuery(id+"F39.wireOp",EDGE,"E84")])],"isStart":false});
            var sketch = newSketch(context, id + "F41", { "sketchPlane" : qUnion([Q0])});
            skCircle(sketch, "E85.0", {"center": v(56.67, -612.5) * mm, "radius": 4 * mm});
            skLineSegment(sketch, "E86", {"start": v(66.3, -612.5) * mm, "end": v(66.3, -600) * mm});
            skPoint(sketch, "E86.startSnap0", {"position": v(66.67, -612.5) * mm});
            skLineSegment(sketch, "E87", {"start": v(66.3, -600) * mm, "end": v(47.03, -600) * mm});
            skLineSegment(sketch, "E88", {"start": v(47.03, -600) * mm, "end": v(47.03, -612.5) * mm});
            skArc(sketch, "E89", {"start": v(66.3, -612.5) * mm, "mid": v(56.67, -622.14) * mm, "end": v(47.03, -612.5) * mm});
            skSolve(sketch);
        }
        {
            var Q0;
            Q0 = qSketchRegion(id + "F41", true);
            extrude(context, id + "F42", {"entities" : qUnion([Q0]), "depth" : 25 * mm});
        }
        {
            var Q0;
            Q0=makeQuery(id+"F42.opExtrude","CAP_FACE",FACE,{"disambiguationData":[OSD([sQuery(id+"F41.wireOp",EDGE,"E85.0"),sQuery(id+"F41.wireOp",EDGE,"E86"),sQuery(id+"F41.wireOp",EDGE,"E87"),sQuery(id+"F41.wireOp",EDGE,"E88"),sQuery(id+"F41.wireOp",EDGE,"E89")])],"isStart":false});
            var sketch = newSketch(context, id + "F43", { "sketchPlane" : qUnion([Q0])});
            skCircle(sketch, "E90.0", {"center": v(56.67, -612.5) * mm, "radius": 4 * mm});
            skSolve(sketch);
        }
        {
            var Q0;
            Q0 = qSketchRegion(id + "F43", true);
            var Q1;
            Q1=makeQuery(id+"F40.opExtrude","CAP_FACE",FACE,{"disambiguationData":[OSD([sQuery(id+"F39.wireOp",EDGE,"E79"),sQuery(id+"F39.wireOp",EDGE,"E81.0"),sQuery(id+"F39.wireOp",EDGE,"E82"),sQuery(id+"F39.wireOp",EDGE,"E83"),sQuery(id+"F39.wireOp",EDGE,"E84")])],"isStart":true});
            extrude(context, id + "F44", {"entities" : qUnion([Q0]), "endBound" : BoundingType.UP_TO_SURFACE, "oppositeDirection" : true, "endBoundEntityFace" : qUnion([Q1]), "depth" : 25 * mm});
        }
        {
            var Q0;
            Q0=makeQuery(id+"F34.opExtrude","SWEPT_FACE",FACE,{"disambiguationData":[OSD([sQuery(id+"F33.wireOp",EDGE,"E65.bottom")])]});
            var Q1;
            Q1=makeQuery(id+"F34.opExtrude","SWEPT_FACE",FACE,{"disambiguationData":[OSD([sQuery(id+"F33.wireOp",EDGE,"E65.top")])]});
            cPlane(context, id + "F45", {"entities" : qUnion([Q0, Q1]), "cplaneType" : CPlaneType.MID_PLANE, "offset" : 25 * mm, "width" : 150 * mm, "height" : 150 * mm});
        }
        {
            var Q0;
            Q0=makeQuery(id+"F40.opExtrude","SWEPT_BODY",BODY,{"disambiguationData":[OSD([sQuery(id+"F39.wireOp",EDGE,"E79"),sQuery(id+"F39.wireOp",EDGE,"E81.0"),sQuery(id+"F39.wireOp",EDGE,"E82"),sQuery(id+"F39.wireOp",EDGE,"E83"),sQuery(id+"F39.wireOp",EDGE,"E84")])]});
            var Q1;
            Q1=makeQuery(id+"F42.opExtrude","SWEPT_BODY",BODY,{"disambiguationData":[OSD([sQuery(id+"F41.wireOp",EDGE,"E85.0"),sQuery(id+"F41.wireOp",EDGE,"E86"),sQuery(id+"F41.wireOp",EDGE,"E87"),sQuery(id+"F41.wireOp",EDGE,"E88"),sQuery(id+"F41.wireOp",EDGE,"E89")])]});
            var Q2;
            Q2=makeQuery(id+"F44.opExtrude","SWEPT_BODY",BODY,{"disambiguationData":[OSD([sQuery(id+"F43.wireOp",EDGE,"E90.0")])]});
            var Q3;
            Q3=qCreatedBy(id+"F45.planeOp",FACE);
            mirror(context, id + "F46", {"entities" : qUnion([Q0, Q1, Q2]), "mirrorPlane" : qUnion([Q3])});
        }
        {
            var Q0;
            Q0=makeQuery(id+"F34.opExtrude","SWEPT_FACE",FACE,{"disambiguationData":[OSD([sQuery(id+"F33.wireOp",EDGE,"E65.right")])]});
            var Q1;
            Q1=makeQuery(id+"F34.opExtrude","SWEPT_FACE",FACE,{"disambiguationData":[OSD([sQuery(id+"F33.wireOp",EDGE,"E66.left")])]});
            cPlane(context, id + "F47", {"entities" : qUnion([Q0, Q1]), "cplaneType" : CPlaneType.MID_PLANE, "offset" : 25 * mm, "width" : 150 * mm, "height" : 150 * mm});
        }
        {
            var Q0;
            Q0=makeQuery(id+"F46.opPattern","COPY",BODY,{"derivedFrom":makeQuery(id+"F40.opExtrude","SWEPT_BODY",BODY,{"disambiguationData":[OSD([sQuery(id+"F39.wireOp",EDGE,"E79"),sQuery(id+"F39.wireOp",EDGE,"E81.0"),sQuery(id+"F39.wireOp",EDGE,"E82"),sQuery(id+"F39.wireOp",EDGE,"E83"),sQuery(id+"F39.wireOp",EDGE,"E84")])]}),"instanceName":"1"});
            var Q1;
            Q1=makeQuery(id+"F40.opExtrude","SWEPT_BODY",BODY,{"disambiguationData":[OSD([sQuery(id+"F39.wireOp",EDGE,"E79"),sQuery(id+"F39.wireOp",EDGE,"E81.0"),sQuery(id+"F39.wireOp",EDGE,"E82"),sQuery(id+"F39.wireOp",EDGE,"E83"),sQuery(id+"F39.wireOp",EDGE,"E84")])]});
            var Q2;
            Q2=makeQuery(id+"F46.opPattern","COPY",BODY,{"derivedFrom":makeQuery(id+"F42.opExtrude","SWEPT_BODY",BODY,{"disambiguationData":[OSD([sQuery(id+"F41.wireOp",EDGE,"E85.0"),sQuery(id+"F41.wireOp",EDGE,"E86"),sQuery(id+"F41.wireOp",EDGE,"E87"),sQuery(id+"F41.wireOp",EDGE,"E88"),sQuery(id+"F41.wireOp",EDGE,"E89")])]}),"instanceName":"1"});
            var Q3;
            Q3=makeQuery(id+"F46.opPattern","COPY",BODY,{"derivedFrom":makeQuery(id+"F44.opExtrude","SWEPT_BODY",BODY,{"disambiguationData":[OSD([sQuery(id+"F43.wireOp",EDGE,"E90.0")])]}),"instanceName":"1"});
            var Q4;
            Q4=makeQuery(id+"F42.opExtrude","SWEPT_BODY",BODY,{"disambiguationData":[OSD([sQuery(id+"F41.wireOp",EDGE,"E85.0"),sQuery(id+"F41.wireOp",EDGE,"E86"),sQuery(id+"F41.wireOp",EDGE,"E87"),sQuery(id+"F41.wireOp",EDGE,"E88"),sQuery(id+"F41.wireOp",EDGE,"E89")])]});
            var Q5;
            Q5=makeQuery(id+"F44.opExtrude","SWEPT_BODY",BODY,{"disambiguationData":[OSD([sQuery(id+"F43.wireOp",EDGE,"E90.0")])]});
            var Q6;
            Q6=qCreatedBy(id+"F47.planeOp",FACE);
            mirror(context, id + "F48", {"entities" : qUnion([Q0, Q1, Q2, Q3, Q4, Q5]), "mirrorPlane" : qUnion([Q6])});
        }
        {
            var Q0;
            Q0=makeQuery(id+"F13.opExtrude","CAP_FACE",FACE,{"disambiguationData":[OSD([sQuery(id+"F12.wireOp",EDGE,"E16.bottom"),sQuery(id+"F12.wireOp",EDGE,"E16.top"),sQuery(id+"F12.wireOp",EDGE,"E16.left"),sQuery(id+"F12.wireOp",EDGE,"E16.right")])],"isStart":false});
            var sketch = newSketch(context, id + "F49", { "sketchPlane" : qUnion([Q0])});
            skCircle(sketch, "E91", {"center": v(-870.83, 630) * mm, "radius": 45 * mm});
            skPoint(sketch, "E91.centerSnap0", {"position": v(-1108.33, 630) * mm});
            skPoint(sketch, "E91.centerSnap1", {"position": v(-870.83, 795) * mm});
            skCircle(sketch, "E92", {"center": v(-1058.33, 745) * mm, "radius": 15 * mm});
            skCircle(sketch, "E93", {"center": v(-1058.33, 630) * mm, "radius": 15 * mm});
            skCircle(sketch, "E94", {"center": v(-1058.33, 515) * mm, "radius": 15 * mm});
            skCircle(sketch, "E95", {"center": v(-691.81, 745) * mm, "radius": 15 * mm});
            skCircle(sketch, "E96", {"center": v(-691.81, 630) * mm, "radius": 15 * mm});
            skCircle(sketch, "E97", {"center": v(-683.33, 515) * mm, "radius": 15 * mm});
            skCircle(sketch, "E98", {"center": v(-319.17, 630) * mm, "radius": 45 * mm});
            skCircle(sketch, "E99", {"center": v(-506.67, 745) * mm, "radius": 15 * mm});
            skCircle(sketch, "E100", {"center": v(-506.67, 630) * mm, "radius": 15 * mm});
            skCircle(sketch, "E101", {"center": v(-506.67, 515) * mm, "radius": 15 * mm});
            skCircle(sketch, "E102", {"center": v(-131.67, 630) * mm, "radius": 15 * mm});
            skCircle(sketch, "E103", {"center": v(-131.67, 745) * mm, "radius": 15 * mm});
            skCircle(sketch, "E104", {"center": v(-131.67, 515) * mm, "radius": 15 * mm});
            skCircle(sketch, "E105", {"center": v(-319.17, 515) * mm, "radius": 15 * mm});
            skCircle(sketch, "E106", {"center": v(-319.17, 745) * mm, "radius": 15 * mm});
            skCircle(sketch, "E107", {"center": v(-870.83, 745) * mm, "radius": 15 * mm});
            skCircle(sketch, "E108", {"center": v(-870.83, 515) * mm, "radius": 15 * mm});
            skLineSegment(sketch, "E109", {"start": v(-1108.33, 630) * mm, "end": v(-633.33, 630) * mm, "construction": true});
            skLineSegment(sketch, "E110", {"start": v(-633.33, 630) * mm, "end": v(-59.48, 630) * mm, "construction": true});
            skLineSegment(sketch, "E111", {"start": v(-319.17, 820.38) * mm, "end": v(-319.17, 430.68) * mm, "construction": true});
            skSolve(sketch);
        }
        {
            var Q0;
            Q0 = qSketchRegion(id + "F49", true);
            extrude(context, id + "F50", {"entities" : qUnion([Q0]), "operationType" : NewBodyOperationType.REMOVE, "oppositeDirection" : true, "depth" : 25 * mm});
        }
        {
            var Q0;
            Q0=makeQuery(id+"F13.opExtrude","CAP_FACE",FACE,{"disambiguationData":[OSD([sQuery(id+"F12.wireOp",EDGE,"E16.bottom"),sQuery(id+"F12.wireOp",EDGE,"E16.top"),sQuery(id+"F12.wireOp",EDGE,"E16.left"),sQuery(id+"F12.wireOp",EDGE,"E16.right")])],"isStart":false});
            var sketch = newSketch(context, id + "F51", { "sketchPlane" : qUnion([Q0])});
            skCircle(sketch, "E112.0", {"center": v(-870.83, 630) * mm, "radius": 45 * mm, "construction": true});
            skCircle(sketch, "E113", {"center": v(-870.83, 630) * mm, "radius": 21.26 * mm});
            skLineSegment(sketch, "E114.bottom", {"start": v(-870.33, 650) * mm, "end": v(-871.33, 650) * mm});
            skLineSegment(sketch, "E114.top", {"start": v(-870.33, 700) * mm, "end": v(-871.33, 700) * mm});
            skLineSegment(sketch, "E114.left", {"start": v(-870.33, 650) * mm, "end": v(-870.33, 700) * mm});
            skLineSegment(sketch, "E114.right", {"start": v(-871.33, 650) * mm, "end": v(-871.33, 700) * mm});
            skPoint(sketch, "E114.middle", {"position": v(-870.83, 675) * mm});
            skLineSegment(sketch, "E115.1.0", {"start": v(-876.54, 649.18) * mm, "end": v(-891.99, 696.73) * mm});
            skLineSegment(sketch, "E115.1.1", {"start": v(-877.49, 648.87) * mm, "end": v(-892.94, 696.42) * mm});
            skPoint(sketch, "E115.1.2", {"position": v(-884.74, 672.8) * mm});
            skLineSegment(sketch, "E115.1.3", {"start": v(-876.54, 649.18) * mm, "end": v(-877.49, 648.87) * mm});
            skLineSegment(sketch, "E115.1.4", {"start": v(-891.99, 696.73) * mm, "end": v(-892.94, 696.42) * mm});
            skLineSegment(sketch, "E115.2.0", {"start": v(-882.18, 646.47) * mm, "end": v(-911.57, 686.93) * mm});
            skLineSegment(sketch, "E115.2.1", {"start": v(-883, 645.89) * mm, "end": v(-912.38, 686.34) * mm});
            skPoint(sketch, "E115.2.2", {"position": v(-897.28, 666.4) * mm});
            skLineSegment(sketch, "E115.2.3", {"start": v(-882.18, 646.47) * mm, "end": v(-883, 645.89) * mm});
            skLineSegment(sketch, "E115.2.4", {"start": v(-911.57, 686.93) * mm, "end": v(-912.38, 686.34) * mm});
            skLineSegment(sketch, "E115.3.0", {"start": v(-886.72, 642.16) * mm, "end": v(-927.17, 671.55) * mm});
            skLineSegment(sketch, "E115.3.1", {"start": v(-887.3, 641.35) * mm, "end": v(-927.76, 670.74) * mm});
            skPoint(sketch, "E115.3.2", {"position": v(-907.24, 656.45) * mm});
            skLineSegment(sketch, "E115.3.3", {"start": v(-886.72, 642.16) * mm, "end": v(-887.3, 641.35) * mm});
            skLineSegment(sketch, "E115.3.4", {"start": v(-927.17, 671.55) * mm, "end": v(-927.76, 670.74) * mm});
            skLineSegment(sketch, "E115.4.0", {"start": v(-889.7, 636.66) * mm, "end": v(-937.25, 652.1) * mm});
            skLineSegment(sketch, "E115.4.1", {"start": v(-890, 635.7) * mm, "end": v(-937.56, 651.16) * mm});
            skPoint(sketch, "E115.4.2", {"position": v(-913.63, 643.9) * mm});
            skLineSegment(sketch, "E115.4.3", {"start": v(-889.7, 636.66) * mm, "end": v(-890, 635.7) * mm});
            skLineSegment(sketch, "E115.4.4", {"start": v(-937.25, 652.1) * mm, "end": v(-937.56, 651.16) * mm});
            skLineSegment(sketch, "E115.5.0", {"start": v(-890.83, 630.5) * mm, "end": v(-940.83, 630.5) * mm});
            skLineSegment(sketch, "E115.5.1", {"start": v(-890.83, 629.5) * mm, "end": v(-940.83, 629.5) * mm});
            skPoint(sketch, "E115.5.2", {"position": v(-915.83, 630) * mm});
            skLineSegment(sketch, "E115.5.3", {"start": v(-890.83, 630.5) * mm, "end": v(-890.83, 629.5) * mm});
            skLineSegment(sketch, "E115.5.4", {"start": v(-940.83, 630.5) * mm, "end": v(-940.83, 629.5) * mm});
            skLineSegment(sketch, "E115.6.0", {"start": v(-890, 624.3) * mm, "end": v(-937.56, 608.84) * mm});
            skLineSegment(sketch, "E115.6.1", {"start": v(-889.7, 623.34) * mm, "end": v(-937.25, 607.9) * mm});
            skPoint(sketch, "E115.6.2", {"position": v(-913.63, 616.1) * mm});
            skLineSegment(sketch, "E115.6.3", {"start": v(-890, 624.3) * mm, "end": v(-889.7, 623.34) * mm});
            skLineSegment(sketch, "E115.6.4", {"start": v(-937.56, 608.84) * mm, "end": v(-937.25, 607.9) * mm});
            skLineSegment(sketch, "E115.7.0", {"start": v(-887.3, 618.65) * mm, "end": v(-927.76, 589.26) * mm});
            skLineSegment(sketch, "E115.7.1", {"start": v(-886.72, 617.84) * mm, "end": v(-927.17, 588.45) * mm});
            skPoint(sketch, "E115.7.2", {"position": v(-907.24, 603.55) * mm});
            skLineSegment(sketch, "E115.7.3", {"start": v(-887.3, 618.65) * mm, "end": v(-886.72, 617.84) * mm});
            skLineSegment(sketch, "E115.7.4", {"start": v(-927.76, 589.26) * mm, "end": v(-927.17, 588.45) * mm});
            skLineSegment(sketch, "E115.8.0", {"start": v(-883, 614.11) * mm, "end": v(-912.38, 573.66) * mm});
            skLineSegment(sketch, "E115.8.1", {"start": v(-882.18, 613.53) * mm, "end": v(-911.57, 573.07) * mm});
            skPoint(sketch, "E115.8.2", {"position": v(-897.28, 593.6) * mm});
            skLineSegment(sketch, "E115.8.3", {"start": v(-883, 614.11) * mm, "end": v(-882.18, 613.53) * mm});
            skLineSegment(sketch, "E115.8.4", {"start": v(-912.38, 573.66) * mm, "end": v(-911.57, 573.07) * mm});
            skLineSegment(sketch, "E115.9.0", {"start": v(-877.49, 611.13) * mm, "end": v(-892.94, 563.58) * mm});
            skLineSegment(sketch, "E115.9.1", {"start": v(-876.54, 610.82) * mm, "end": v(-891.99, 563.27) * mm});
            skPoint(sketch, "E115.9.2", {"position": v(-884.74, 587.2) * mm});
            skLineSegment(sketch, "E115.9.3", {"start": v(-877.49, 611.13) * mm, "end": v(-876.54, 610.82) * mm});
            skLineSegment(sketch, "E115.9.4", {"start": v(-892.94, 563.58) * mm, "end": v(-891.99, 563.27) * mm});
            skLineSegment(sketch, "E115.10.0", {"start": v(-871.33, 610) * mm, "end": v(-871.33, 560) * mm});
            skLineSegment(sketch, "E115.10.1", {"start": v(-870.33, 610) * mm, "end": v(-870.33, 560) * mm});
            skPoint(sketch, "E115.10.2", {"position": v(-870.83, 585) * mm});
            skLineSegment(sketch, "E115.10.3", {"start": v(-871.33, 610) * mm, "end": v(-870.33, 610) * mm});
            skLineSegment(sketch, "E115.10.4", {"start": v(-871.33, 560) * mm, "end": v(-870.33, 560) * mm});
            skLineSegment(sketch, "E115.11.0", {"start": v(-865.13, 610.82) * mm, "end": v(-849.68, 563.27) * mm});
            skLineSegment(sketch, "E115.11.1", {"start": v(-864.18, 611.13) * mm, "end": v(-848.73, 563.58) * mm});
            skPoint(sketch, "E115.11.2", {"position": v(-856.93, 587.2) * mm});
            skLineSegment(sketch, "E115.11.3", {"start": v(-865.13, 610.82) * mm, "end": v(-864.18, 611.13) * mm});
            skLineSegment(sketch, "E115.11.4", {"start": v(-849.68, 563.27) * mm, "end": v(-848.73, 563.58) * mm});
            skLineSegment(sketch, "E115.12.0", {"start": v(-859.48, 613.53) * mm, "end": v(-830.1, 573.07) * mm});
            skLineSegment(sketch, "E115.12.1", {"start": v(-858.67, 614.11) * mm, "end": v(-829.28, 573.66) * mm});
            skPoint(sketch, "E115.12.2", {"position": v(-844.38, 593.6) * mm});
            skLineSegment(sketch, "E115.12.3", {"start": v(-859.48, 613.53) * mm, "end": v(-858.67, 614.11) * mm});
            skLineSegment(sketch, "E115.12.4", {"start": v(-830.1, 573.07) * mm, "end": v(-829.28, 573.66) * mm});
            skLineSegment(sketch, "E115.13.0", {"start": v(-854.95, 617.84) * mm, "end": v(-814.5, 588.45) * mm});
            skLineSegment(sketch, "E115.13.1", {"start": v(-854.36, 618.65) * mm, "end": v(-813.9, 589.26) * mm});
            skPoint(sketch, "E115.13.2", {"position": v(-834.43, 603.55) * mm});
            skLineSegment(sketch, "E115.13.3", {"start": v(-854.95, 617.84) * mm, "end": v(-854.36, 618.65) * mm});
            skLineSegment(sketch, "E115.13.4", {"start": v(-814.5, 588.45) * mm, "end": v(-813.9, 589.26) * mm});
            skLineSegment(sketch, "E115.14.0", {"start": v(-851.97, 623.34) * mm, "end": v(-804.41, 607.9) * mm});
            skLineSegment(sketch, "E115.14.1", {"start": v(-851.66, 624.3) * mm, "end": v(-804.1, 608.84) * mm});
            skPoint(sketch, "E115.14.2", {"position": v(-828.04, 616.1) * mm});
            skLineSegment(sketch, "E115.14.3", {"start": v(-851.97, 623.34) * mm, "end": v(-851.66, 624.3) * mm});
            skLineSegment(sketch, "E115.14.4", {"start": v(-804.41, 607.9) * mm, "end": v(-804.1, 608.84) * mm});
            skLineSegment(sketch, "E115.15.0", {"start": v(-850.83, 629.5) * mm, "end": v(-800.83, 629.5) * mm});
            skLineSegment(sketch, "E115.15.1", {"start": v(-850.83, 630.5) * mm, "end": v(-800.83, 630.5) * mm});
            skPoint(sketch, "E115.15.2", {"position": v(-825.83, 630) * mm});
            skLineSegment(sketch, "E115.15.3", {"start": v(-850.83, 629.5) * mm, "end": v(-850.83, 630.5) * mm});
            skLineSegment(sketch, "E115.15.4", {"start": v(-800.83, 629.5) * mm, "end": v(-800.83, 630.5) * mm});
            skLineSegment(sketch, "E115.16.0", {"start": v(-851.66, 635.7) * mm, "end": v(-804.1, 651.16) * mm});
            skLineSegment(sketch, "E115.16.1", {"start": v(-851.97, 636.66) * mm, "end": v(-804.41, 652.1) * mm});
            skPoint(sketch, "E115.16.2", {"position": v(-828.04, 643.9) * mm});
            skLineSegment(sketch, "E115.16.3", {"start": v(-851.66, 635.7) * mm, "end": v(-851.97, 636.66) * mm});
            skLineSegment(sketch, "E115.16.4", {"start": v(-804.1, 651.16) * mm, "end": v(-804.41, 652.1) * mm});
            skLineSegment(sketch, "E115.17.0", {"start": v(-854.36, 641.35) * mm, "end": v(-813.9, 670.74) * mm});
            skLineSegment(sketch, "E115.17.1", {"start": v(-854.95, 642.16) * mm, "end": v(-814.5, 671.55) * mm});
            skPoint(sketch, "E115.17.2", {"position": v(-834.43, 656.45) * mm});
            skLineSegment(sketch, "E115.17.3", {"start": v(-854.36, 641.35) * mm, "end": v(-854.95, 642.16) * mm});
            skLineSegment(sketch, "E115.17.4", {"start": v(-813.9, 670.74) * mm, "end": v(-814.5, 671.55) * mm});
            skLineSegment(sketch, "E115.18.0", {"start": v(-858.67, 645.89) * mm, "end": v(-829.28, 686.34) * mm});
            skLineSegment(sketch, "E115.18.1", {"start": v(-859.48, 646.47) * mm, "end": v(-830.1, 686.93) * mm});
            skPoint(sketch, "E115.18.2", {"position": v(-844.38, 666.4) * mm});
            skLineSegment(sketch, "E115.18.3", {"start": v(-858.67, 645.89) * mm, "end": v(-859.48, 646.47) * mm});
            skLineSegment(sketch, "E115.18.4", {"start": v(-829.28, 686.34) * mm, "end": v(-830.1, 686.93) * mm});
            skLineSegment(sketch, "E115.19.0", {"start": v(-864.18, 648.87) * mm, "end": v(-848.73, 696.42) * mm});
            skLineSegment(sketch, "E115.19.1", {"start": v(-865.13, 649.18) * mm, "end": v(-849.68, 696.73) * mm});
            skPoint(sketch, "E115.19.2", {"position": v(-856.93, 672.8) * mm});
            skLineSegment(sketch, "E115.19.3", {"start": v(-864.18, 648.87) * mm, "end": v(-865.13, 649.18) * mm});
            skLineSegment(sketch, "E115.19.4", {"start": v(-848.73, 696.42) * mm, "end": v(-849.68, 696.73) * mm});
            skSolve(sketch);
        }
        {
            var Q0;
            Q0 = qSketchRegion(id + "F51", true);
            extrude(context, id + "F52", {"entities" : qUnion([Q0]), "depth" : 40 * mm});
        }
        {
            var Q0;
            Q0=makeQuery(id+"F52.opExtrude","SWEPT_BODY",BODY,{"disambiguationData":[OSD([sQuery(id+"F51.wireOp",EDGE,"E113"),sQuery(id+"F51.wireOp",EDGE,"E114.top"),sQuery(id+"F51.wireOp",EDGE,"E114.left"),sQuery(id+"F51.wireOp",EDGE,"E114.right"),sQuery(id+"F51.wireOp",EDGE,"E115.1.0"),sQuery(id+"F51.wireOp",EDGE,"E115.1.1"),sQuery(id+"F51.wireOp",EDGE,"E115.1.4"),sQuery(id+"F51.wireOp",EDGE,"E115.2.0"),sQuery(id+"F51.wireOp",EDGE,"E115.2.1"),sQuery(id+"F51.wireOp",EDGE,"E115.2.4"),sQuery(id+"F51.wireOp",EDGE,"E115.3.0"),sQuery(id+"F51.wireOp",EDGE,"E115.3.1"),sQuery(id+"F51.wireOp",EDGE,"E115.3.4"),sQuery(id+"F51.wireOp",EDGE,"E115.4.0"),sQuery(id+"F51.wireOp",EDGE,"E115.4.1"),sQuery(id+"F51.wireOp",EDGE,"E115.4.4"),sQuery(id+"F51.wireOp",EDGE,"E115.5.0"),sQuery(id+"F51.wireOp",EDGE,"E115.5.1"),sQuery(id+"F51.wireOp",EDGE,"E115.5.4"),sQuery(id+"F51.wireOp",EDGE,"E115.6.0"),sQuery(id+"F51.wireOp",EDGE,"E115.6.1"),sQuery(id+"F51.wireOp",EDGE,"E115.6.4"),sQuery(id+"F51.wireOp",EDGE,"E115.7.0"),sQuery(id+"F51.wireOp",EDGE,"E115.7.1"),sQuery(id+"F51.wireOp",EDGE,"E115.7.4"),sQuery(id+"F51.wireOp",EDGE,"E115.8.0"),sQuery(id+"F51.wireOp",EDGE,"E115.8.1"),sQuery(id+"F51.wireOp",EDGE,"E115.8.4"),sQuery(id+"F51.wireOp",EDGE,"E115.9.0"),sQuery(id+"F51.wireOp",EDGE,"E115.9.1"),sQuery(id+"F51.wireOp",EDGE,"E115.9.4"),sQuery(id+"F51.wireOp",EDGE,"E115.10.0"),sQuery(id+"F51.wireOp",EDGE,"E115.10.1"),sQuery(id+"F51.wireOp",EDGE,"E115.10.4"),sQuery(id+"F51.wireOp",EDGE,"E115.11.0"),sQuery(id+"F51.wireOp",EDGE,"E115.11.1"),sQuery(id+"F51.wireOp",EDGE,"E115.11.4"),sQuery(id+"F51.wireOp",EDGE,"E115.12.0"),sQuery(id+"F51.wireOp",EDGE,"E115.12.1"),sQuery(id+"F51.wireOp",EDGE,"E115.12.4"),sQuery(id+"F51.wireOp",EDGE,"E115.13.0"),sQuery(id+"F51.wireOp",EDGE,"E115.13.1"),sQuery(id+"F51.wireOp",EDGE,"E115.13.4"),sQuery(id+"F51.wireOp",EDGE,"E115.14.0"),sQuery(id+"F51.wireOp",EDGE,"E115.14.1"),sQuery(id+"F51.wireOp",EDGE,"E115.14.4"),sQuery(id+"F51.wireOp",EDGE,"E115.15.0"),sQuery(id+"F51.wireOp",EDGE,"E115.15.1"),sQuery(id+"F51.wireOp",EDGE,"E115.15.4"),sQuery(id+"F51.wireOp",EDGE,"E115.16.0"),sQuery(id+"F51.wireOp",EDGE,"E115.16.1"),sQuery(id+"F51.wireOp",EDGE,"E115.16.4"),sQuery(id+"F51.wireOp",EDGE,"E115.17.0"),sQuery(id+"F51.wireOp",EDGE,"E115.17.1"),sQuery(id+"F51.wireOp",EDGE,"E115.17.4"),sQuery(id+"F51.wireOp",EDGE,"E115.18.0"),sQuery(id+"F51.wireOp",EDGE,"E115.18.1"),sQuery(id+"F51.wireOp",EDGE,"E115.18.4"),sQuery(id+"F51.wireOp",EDGE,"E115.19.0"),sQuery(id+"F51.wireOp",EDGE,"E115.19.1"),sQuery(id+"F51.wireOp",EDGE,"E115.19.4")])]});
            var Q1;
            Q1=qCreatedBy(id+"F47.planeOp",FACE);
            mirror(context, id + "F53", {"entities" : qUnion([Q0]), "mirrorPlane" : qUnion([Q1])});
        }
        {
            var Q0;
            Q0=makeQuery(id+"F52.opExtrude","CAP_FACE",FACE,{"disambiguationData":[OSD([sQuery(id+"F51.wireOp",EDGE,"E113"),sQuery(id+"F51.wireOp",EDGE,"E114.top"),sQuery(id+"F51.wireOp",EDGE,"E114.left"),sQuery(id+"F51.wireOp",EDGE,"E114.right"),sQuery(id+"F51.wireOp",EDGE,"E115.1.0"),sQuery(id+"F51.wireOp",EDGE,"E115.1.1"),sQuery(id+"F51.wireOp",EDGE,"E115.1.4"),sQuery(id+"F51.wireOp",EDGE,"E115.2.0"),sQuery(id+"F51.wireOp",EDGE,"E115.2.1"),sQuery(id+"F51.wireOp",EDGE,"E115.2.4"),sQuery(id+"F51.wireOp",EDGE,"E115.3.0"),sQuery(id+"F51.wireOp",EDGE,"E115.3.1"),sQuery(id+"F51.wireOp",EDGE,"E115.3.4"),sQuery(id+"F51.wireOp",EDGE,"E115.4.0"),sQuery(id+"F51.wireOp",EDGE,"E115.4.1"),sQuery(id+"F51.wireOp",EDGE,"E115.4.4"),sQuery(id+"F51.wireOp",EDGE,"E115.5.0"),sQuery(id+"F51.wireOp",EDGE,"E115.5.1"),sQuery(id+"F51.wireOp",EDGE,"E115.5.4"),sQuery(id+"F51.wireOp",EDGE,"E115.6.0"),sQuery(id+"F51.wireOp",EDGE,"E115.6.1"),sQuery(id+"F51.wireOp",EDGE,"E115.6.4"),sQuery(id+"F51.wireOp",EDGE,"E115.7.0"),sQuery(id+"F51.wireOp",EDGE,"E115.7.1"),sQuery(id+"F51.wireOp",EDGE,"E115.7.4"),sQuery(id+"F51.wireOp",EDGE,"E115.8.0"),sQuery(id+"F51.wireOp",EDGE,"E115.8.1"),sQuery(id+"F51.wireOp",EDGE,"E115.8.4"),sQuery(id+"F51.wireOp",EDGE,"E115.9.0"),sQuery(id+"F51.wireOp",EDGE,"E115.9.1"),sQuery(id+"F51.wireOp",EDGE,"E115.9.4"),sQuery(id+"F51.wireOp",EDGE,"E115.10.0"),sQuery(id+"F51.wireOp",EDGE,"E115.10.1"),sQuery(id+"F51.wireOp",EDGE,"E115.10.4"),sQuery(id+"F51.wireOp",EDGE,"E115.11.0"),sQuery(id+"F51.wireOp",EDGE,"E115.11.1"),sQuery(id+"F51.wireOp",EDGE,"E115.11.4"),sQuery(id+"F51.wireOp",EDGE,"E115.12.0"),sQuery(id+"F51.wireOp",EDGE,"E115.12.1"),sQuery(id+"F51.wireOp",EDGE,"E115.12.4"),sQuery(id+"F51.wireOp",EDGE,"E115.13.0"),sQuery(id+"F51.wireOp",EDGE,"E115.13.1"),sQuery(id+"F51.wireOp",EDGE,"E115.13.4"),sQuery(id+"F51.wireOp",EDGE,"E115.14.0"),sQuery(id+"F51.wireOp",EDGE,"E115.14.1"),sQuery(id+"F51.wireOp",EDGE,"E115.14.4"),sQuery(id+"F51.wireOp",EDGE,"E115.15.0"),sQuery(id+"F51.wireOp",EDGE,"E115.15.1"),sQuery(id+"F51.wireOp",EDGE,"E115.15.4"),sQuery(id+"F51.wireOp",EDGE,"E115.16.0"),sQuery(id+"F51.wireOp",EDGE,"E115.16.1"),sQuery(id+"F51.wireOp",EDGE,"E115.16.4"),sQuery(id+"F51.wireOp",EDGE,"E115.17.0"),sQuery(id+"F51.wireOp",EDGE,"E115.17.1"),sQuery(id+"F51.wireOp",EDGE,"E115.17.4"),sQuery(id+"F51.wireOp",EDGE,"E115.18.0"),sQuery(id+"F51.wireOp",EDGE,"E115.18.1"),sQuery(id+"F51.wireOp",EDGE,"E115.18.4"),sQuery(id+"F51.wireOp",EDGE,"E115.19.0"),sQuery(id+"F51.wireOp",EDGE,"E115.19.1"),sQuery(id+"F51.wireOp",EDGE,"E115.19.4")])],"isStart":false});
            var sketch = newSketch(context, id + "F54", { "sketchPlane" : qUnion([Q0])});
            skCircle(sketch, "E116", {"center": v(-870.83, 630) * mm, "radius": 4 * mm});
            skCircle(sketch, "E117", {"center": v(-319.17, 630) * mm, "radius": 4 * mm});
            skSolve(sketch);
        }
        {
            var Q0;
            Q0 = qSketchRegion(id + "F54", true);
            extrude(context, id + "F55", {"entities" : qUnion([Q0]), "operationType" : NewBodyOperationType.ADD, "depth" : 100 * mm});
        }
        {
            var Q0;
            Q0=makeQuery(id+"F13.opExtrude","CAP_FACE",FACE,{"disambiguationData":[OSD([sQuery(id+"F12.wireOp",EDGE,"E16.bottom"),sQuery(id+"F12.wireOp",EDGE,"E16.top"),sQuery(id+"F12.wireOp",EDGE,"E16.left"),sQuery(id+"F12.wireOp",EDGE,"E16.right")])],"isStart":false});
            var sketch = newSketch(context, id + "F56", { "sketchPlane" : qUnion([Q0])});
            skLineSegment(sketch, "E118.bottom", {"start": v(-1108.33, 795) * mm, "end": v(-633.33, 795) * mm});
            skLineSegment(sketch, "E118.top", {"start": v(-1108.33, 465) * mm, "end": v(-633.33, 465) * mm});
            skLineSegment(sketch, "E118.left", {"start": v(-1108.33, 795) * mm, "end": v(-1108.33, 465) * mm});
            skLineSegment(sketch, "E118.right", {"start": v(-633.33, 795) * mm, "end": v(-633.33, 465) * mm});
            skLineSegment(sketch, "E119.bottom", {"start": v(-556.67, 795) * mm, "end": v(-81.67, 795) * mm});
            skLineSegment(sketch, "E119.top", {"start": v(-556.67, 465) * mm, "end": v(-81.67, 465) * mm});
            skLineSegment(sketch, "E119.left", {"start": v(-556.67, 795) * mm, "end": v(-556.67, 465) * mm});
            skLineSegment(sketch, "E119.right", {"start": v(-81.67, 795) * mm, "end": v(-81.67, 465) * mm});
            skLineSegment(sketch, "E120.bottom", {"start": v(-554.67, 793) * mm, "end": v(-83.67, 793) * mm});
            skLineSegment(sketch, "E120.top", {"start": v(-554.67, 467) * mm, "end": v(-83.67, 467) * mm});
            skLineSegment(sketch, "E120.left", {"start": v(-554.67, 793) * mm, "end": v(-554.67, 467) * mm});
            skLineSegment(sketch, "E120.right", {"start": v(-83.67, 793) * mm, "end": v(-83.67, 467) * mm});
            skLineSegment(sketch, "E121.bottom", {"start": v(-1106.33, 793) * mm, "end": v(-635.33, 793) * mm});
            skLineSegment(sketch, "E121.top", {"start": v(-1106.33, 467) * mm, "end": v(-635.33, 467) * mm});
            skLineSegment(sketch, "E121.left", {"start": v(-1106.33, 793) * mm, "end": v(-1106.33, 467) * mm});
            skLineSegment(sketch, "E121.right", {"start": v(-635.33, 793) * mm, "end": v(-635.33, 467) * mm});
            skSolve(sketch);
        }
        {
            var Q0;
            Q0 = qSketchRegion(id + "F56", true);
            extrude(context, id + "F57", {"entities" : qUnion([Q0]), "depth" : 80 * mm});
        }
        {
            var Q0;
            Q0=makeQuery(id+"F57.opExtrude","CAP_FACE",FACE,{"disambiguationData":[OSD([sQuery(id+"F56.wireOp",EDGE,"E118.bottom"),sQuery(id+"F56.wireOp",EDGE,"E118.top"),sQuery(id+"F56.wireOp",EDGE,"E118.left"),sQuery(id+"F56.wireOp",EDGE,"E118.right"),sQuery(id+"F56.wireOp",EDGE,"E121.bottom"),sQuery(id+"F56.wireOp",EDGE,"E121.top"),sQuery(id+"F56.wireOp",EDGE,"E121.left"),sQuery(id+"F56.wireOp",EDGE,"E121.right")])],"isStart":false});
            var sketch = newSketch(context, id + "F58", { "sketchPlane" : qUnion([Q0])});
            skLineSegment(sketch, "E122.bottom", {"start": v(-1108.33, 795) * mm, "end": v(-633.33, 795) * mm});
            skLineSegment(sketch, "E122.top", {"start": v(-1108.33, 465) * mm, "end": v(-633.33, 465) * mm});
            skLineSegment(sketch, "E122.left", {"start": v(-1108.33, 795) * mm, "end": v(-1108.33, 465) * mm});
            skLineSegment(sketch, "E122.right", {"start": v(-633.33, 795) * mm, "end": v(-633.33, 465) * mm});
            skLineSegment(sketch, "E123.bottom", {"start": v(-556.67, 795) * mm, "end": v(-81.67, 795) * mm});
            skLineSegment(sketch, "E123.top", {"start": v(-556.67, 465) * mm, "end": v(-81.67, 465) * mm});
            skLineSegment(sketch, "E123.left", {"start": v(-556.67, 795) * mm, "end": v(-556.67, 465) * mm});
            skLineSegment(sketch, "E123.right", {"start": v(-81.67, 795) * mm, "end": v(-81.67, 465) * mm});
            skSolve(sketch);
        }
        {
            var Q0;
            Q0 = qSketchRegion(id + "F58", true);
            extrude(context, id + "F59", {"entities" : qUnion([Q0]), "depth" : 2 * mm});
        }
        {
            var Q0;
            Q0=makeQuery(id+"F7.opShell","OFFSET_FACE",FACE,{"disambiguationData":[OSD([sQuery(id+"F5.wireOp",EDGE,"E0.top")])]});
            var sketch = newSketch(context, id + "F60", { "sketchPlane" : qUnion([Q0])});
            skCircle(sketch, "E124.0", {"center": v(-870.83, 630) * mm, "radius": 45 * mm, "construction": true});
            skCircle(sketch, "E125.0", {"center": v(-319.17, 630) * mm, "radius": 45 * mm, "construction": true});
            skLineSegment(sketch, "E126.bottom", {"start": v(-638.33, 432) * mm, "end": v(-1103.33, 432) * mm});
            skLineSegment(sketch, "E126.top", {"start": v(-638.33, 828) * mm, "end": v(-1103.33, 828) * mm});
            skLineSegment(sketch, "E126.left", {"start": v(-600.33, 470) * mm, "end": v(-600.33, 790) * mm});
            skLineSegment(sketch, "E126.right", {"start": v(-1141.33, 470) * mm, "end": v(-1141.33, 790) * mm});
            skLineSegment(sketch, "E127.bottom", {"start": v(-86.67, 432) * mm, "end": v(-551.67, 432) * mm});
            skLineSegment(sketch, "E127.top", {"start": v(-86.67, 828) * mm, "end": v(-551.67, 828) * mm});
            skLineSegment(sketch, "E127.left", {"start": v(-48.67, 470) * mm, "end": v(-48.67, 790) * mm});
            skLineSegment(sketch, "E127.right", {"start": v(-589.67, 470) * mm, "end": v(-589.67, 790) * mm});
            skPoint(sketch, "E128.visualSharp", {"position": v(-48.67, 828) * mm});
            skArc(sketch, "E128.filletArc", {"start": v(-48.67, 790) * mm, "mid": v(-59.8, 816.87) * mm, "end": v(-86.67, 828) * mm});
            skPoint(sketch, "E129.visualSharp", {"position": v(-48.67, 432) * mm});
            skArc(sketch, "E129.filletArc", {"start": v(-86.67, 432) * mm, "mid": v(-59.8, 443.13) * mm, "end": v(-48.67, 470) * mm});
            skPoint(sketch, "E130.visualSharp", {"position": v(-589.67, 432) * mm});
            skArc(sketch, "E130.filletArc", {"start": v(-589.67, 470) * mm, "mid": v(-578.54, 443.13) * mm, "end": v(-551.67, 432) * mm});
            skPoint(sketch, "E131.visualSharp", {"position": v(-589.67, 828) * mm});
            skArc(sketch, "E131.filletArc", {"start": v(-551.67, 828) * mm, "mid": v(-578.54, 816.87) * mm, "end": v(-589.67, 790) * mm});
            skPoint(sketch, "E132.visualSharp", {"position": v(-600.33, 828) * mm});
            skArc(sketch, "E132.filletArc", {"start": v(-600.33, 790) * mm, "mid": v(-611.46, 816.87) * mm, "end": v(-638.33, 828) * mm});
            skPoint(sketch, "E133.visualSharp", {"position": v(-600.33, 432) * mm});
            skArc(sketch, "E133.filletArc", {"start": v(-638.33, 432) * mm, "mid": v(-611.46, 443.13) * mm, "end": v(-600.33, 470) * mm});
            skPoint(sketch, "E134.visualSharp", {"position": v(-1141.33, 432) * mm});
            skArc(sketch, "E134.filletArc", {"start": v(-1141.33, 470) * mm, "mid": v(-1130.2, 443.13) * mm, "end": v(-1103.33, 432) * mm});
            skPoint(sketch, "E135.visualSharp", {"position": v(-1141.33, 828) * mm});
            skArc(sketch, "E135.filletArc", {"start": v(-1103.33, 828) * mm, "mid": v(-1130.2, 816.87) * mm, "end": v(-1141.33, 790) * mm});
            skLineSegment(sketch, "E136.bottom", {"start": v(-633.33, 465) * mm, "end": v(-1108.33, 465) * mm});
            skLineSegment(sketch, "E136.top", {"start": v(-633.33, 795) * mm, "end": v(-1108.33, 795) * mm});
            skLineSegment(sketch, "E136.left", {"start": v(-633.33, 465) * mm, "end": v(-633.33, 795) * mm});
            skLineSegment(sketch, "E136.right", {"start": v(-1108.33, 465) * mm, "end": v(-1108.33, 795) * mm});
            skLineSegment(sketch, "E137.bottom", {"start": v(-81.67, 465) * mm, "end": v(-556.67, 465) * mm});
            skLineSegment(sketch, "E137.top", {"start": v(-81.67, 795) * mm, "end": v(-556.67, 795) * mm});
            skLineSegment(sketch, "E137.left", {"start": v(-81.67, 465) * mm, "end": v(-81.67, 795) * mm});
            skLineSegment(sketch, "E137.right", {"start": v(-556.67, 465) * mm, "end": v(-556.67, 795) * mm});
            skSolve(sketch);
        }
        {
            var Q0;
            Q0 = qSketchRegion(id + "F60", true);
            var Q1;
            Q1=makeQuery(id+"F59.opExtrude","CAP_FACE",FACE,{"disambiguationData":[OSD([sQuery(id+"F58.wireOp",EDGE,"E123.bottom"),sQuery(id+"F58.wireOp",EDGE,"E123.top"),sQuery(id+"F58.wireOp",EDGE,"E123.left"),sQuery(id+"F58.wireOp",EDGE,"E123.right")])],"isStart":false});
            extrude(context, id + "F61", {"entities" : qUnion([Q0]), "endBound" : BoundingType.UP_TO_SURFACE, "endBoundEntityFace" : qUnion([Q1]), "depth" : 25 * mm});
        }
        {
            var Q0;
            Q0=qCreatedBy(id+"F45.planeOp",FACE);
            var sketch = newSketch(context, id + "F62", { "sketchPlane" : qUnion([Q0])});
            skCircle(sketch, "E138", {"center": v(541.67, -680) * mm, "radius": 15 * mm});
            skCircle(sketch, "E139", {"center": v(541.67, -680) * mm, "radius": 4 * mm});
            skSolve(sketch);
        }
        {
            var Q0;
            Q0 = qSketchRegion(id + "F62", true);
            extrude(context, id + "F63", {"entities" : qUnion([Q0]), "depth" : 150 * mm, "symmetric" : true});
        }
        {
            var Q0;
            Q0=makeQuery(id+"F63.opExtrude","CAP_FACE",FACE,{"disambiguationData":[OSD([sQuery(id+"F62.wireOp",EDGE,"E138"),sQuery(id+"F62.wireOp",EDGE,"E139")])],"isStart":true});
            var sketch = newSketch(context, id + "F64", { "sketchPlane" : qUnion([Q0])});
            skCircle(sketch, "E140.0", {"center": v(541.67, 680) * mm, "radius": 4 * mm});
            skArc(sketch, "E141", {"start": v(526.67, 680) * mm, "mid": v(541.67, 695) * mm, "end": v(556.67, 680) * mm});
            skLineSegment(sketch, "E142", {"start": v(526.67, 680) * mm, "end": v(526.67, 625) * mm});
            skLineSegment(sketch, "E143", {"start": v(526.67, 625) * mm, "end": v(556.67, 625) * mm});
            skLineSegment(sketch, "E144", {"start": v(556.67, 625) * mm, "end": v(556.67, 680) * mm});
            skSolve(sketch);
        }
        {
            var Q0;
            Q0 = qSketchRegion(id + "F64", true);
            extrude(context, id + "F65", {"entities" : qUnion([Q0]), "depth" : 2 * mm});
        }
        {
            var Q0;
            Q0=makeQuery(id+"F65.opExtrude","SWEPT_BODY",BODY,{"disambiguationData":[OSD([sQuery(id+"F64.wireOp",EDGE,"E140.0"),sQuery(id+"F64.wireOp",EDGE,"E141"),sQuery(id+"F64.wireOp",EDGE,"E142"),sQuery(id+"F64.wireOp",EDGE,"E143"),sQuery(id+"F64.wireOp",EDGE,"E144")])]});
            var Q1;
            Q1=qCreatedBy(id+"F45.planeOp",FACE);
            mirror(context, id + "F66", {"entities" : qUnion([Q0]), "mirrorPlane" : qUnion([Q1])});
        }
        {
            var Q0;
            Q0=makeQuery(id+"F65.opExtrude","CAP_FACE",FACE,{"disambiguationData":[OSD([sQuery(id+"F64.wireOp",EDGE,"E140.0"),sQuery(id+"F64.wireOp",EDGE,"E141"),sQuery(id+"F64.wireOp",EDGE,"E142"),sQuery(id+"F64.wireOp",EDGE,"E143"),sQuery(id+"F64.wireOp",EDGE,"E144")])],"isStart":false});
            var sketch = newSketch(context, id + "F67", { "sketchPlane" : qUnion([Q0])});
            skCircle(sketch, "E145.0", {"center": v(541.67, 680) * mm, "radius": 4 * mm});
            skSolve(sketch);
        }
        {
            var Q0;
            Q0 = qSketchRegion(id + "F67", true);
            extrude(context, id + "F68", {"entities" : qUnion([Q0]), "depth" : 5 * mm, "hasSecondDirection" : true, "secondDirectionOppositeDirection" : true, "secondDirectionDepth" : (2 + 150 + 2 + 5) * mm});
        }
        {
            var Q0;
            Q0=makeQuery(id+"F65.opExtrude","SWEPT_BODY",BODY,{"disambiguationData":[OSD([sQuery(id+"F64.wireOp",EDGE,"E140.0"),sQuery(id+"F64.wireOp",EDGE,"E141"),sQuery(id+"F64.wireOp",EDGE,"E142"),sQuery(id+"F64.wireOp",EDGE,"E143"),sQuery(id+"F64.wireOp",EDGE,"E144")])]});
            var Q1;
            Q1=makeQuery(id+"F68.opExtrude","SWEPT_BODY",BODY,{"disambiguationData":[OSD([sQuery(id+"F67.wireOp",EDGE,"E145.0")])]});
            var Q2;
            Q2=makeQuery(id+"F63.opExtrude","SWEPT_BODY",BODY,{"disambiguationData":[OSD([sQuery(id+"F62.wireOp",EDGE,"E138"),sQuery(id+"F62.wireOp",EDGE,"E139")])]});
            var Q3;
            Q3=makeQuery(id+"F66.opPattern","COPY",BODY,{"derivedFrom":makeQuery(id+"F65.opExtrude","SWEPT_BODY",BODY,{"disambiguationData":[OSD([sQuery(id+"F64.wireOp",EDGE,"E140.0"),sQuery(id+"F64.wireOp",EDGE,"E141"),sQuery(id+"F64.wireOp",EDGE,"E142"),sQuery(id+"F64.wireOp",EDGE,"E143"),sQuery(id+"F64.wireOp",EDGE,"E144")])]}),"instanceName":"1"});
            var Q4;
            Q4=qCreatedBy(id+"F47.planeOp",FACE);
            mirror(context, id + "F69", {"entities" : qUnion([Q0, Q1, Q2, Q3]), "mirrorPlane" : qUnion([Q4])});
        }
        {
            var Q0;
            Q0=makeQuery(id+"F32.opExtrude","SWEPT_FACE",FACE,{"disambiguationData":[OSD([sQuery(id+"F31.wireOp",EDGE,"E63.right")])]});
            var Q1;
            Q1=makeQuery(id+"F32.opExtrude","SWEPT_FACE",FACE,{"disambiguationData":[OSD([sQuery(id+"F31.wireOp",EDGE,"E63.left")])]});
            cPlane(context, id + "F70", {"entities" : qUnion([Q0, Q1]), "cplaneType" : CPlaneType.MID_PLANE, "offset" : 25 * mm, "width" : 150 * mm, "height" : 150 * mm});
        }
        {
            var Q0;
            Q0=qCreatedBy(id+"F70.planeOp",FACE);
            var sketch = newSketch(context, id + "F71", { "sketchPlane" : qUnion([Q0])});
            skCircle(sketch, "E146", {"center": v(-665, 345) * mm, "radius": 15 * mm});
            skCircle(sketch, "E147", {"center": v(-665, 345) * mm, "radius": 4 * mm});
            skSolve(sketch);
        }
        {
            var Q0;
            Q0 = qSketchRegion(id + "F71", true);
            extrude(context, id + "F72", {"entities" : qUnion([Q0]), "depth" : 150 * mm, "symmetric" : true});
        }
        {
            var Q0;
            Q0=makeQuery(id+"F72.opExtrude","CAP_FACE",FACE,{"disambiguationData":[OSD([sQuery(id+"F71.wireOp",EDGE,"E146"),sQuery(id+"F71.wireOp",EDGE,"E147")])],"isStart":true});
            var sketch = newSketch(context, id + "F73", { "sketchPlane" : qUnion([Q0])});
            skCircle(sketch, "E148.0", {"center": v(665, 345) * mm, "radius": 4 * mm});
            skArc(sketch, "E149", {"start": v(665, 360) * mm, "mid": v(680, 345) * mm, "end": v(665, 330) * mm});
            skLineSegment(sketch, "E150", {"start": v(665, 360) * mm, "end": v(610, 360) * mm});
            skLineSegment(sketch, "E151", {"start": v(610, 360) * mm, "end": v(610, 330) * mm});
            skLineSegment(sketch, "E152", {"start": v(610, 330) * mm, "end": v(665, 330) * mm});
            skSolve(sketch);
        }
        {
            var Q0;
            Q0 = qSketchRegion(id + "F73", true);
            extrude(context, id + "F74", {"entities" : qUnion([Q0]), "depth" : 2 * mm});
        }
        {
            var Q0;
            Q0=makeQuery(id+"F74.opExtrude","SWEPT_BODY",BODY,{"disambiguationData":[OSD([sQuery(id+"F73.wireOp",EDGE,"E148.0"),sQuery(id+"F73.wireOp",EDGE,"E149"),sQuery(id+"F73.wireOp",EDGE,"E150"),sQuery(id+"F73.wireOp",EDGE,"E151"),sQuery(id+"F73.wireOp",EDGE,"E152")])]});
            var Q1;
            Q1=qCreatedBy(id+"F70.planeOp",FACE);
            mirror(context, id + "F75", {"entities" : qUnion([Q0]), "mirrorPlane" : qUnion([Q1])});
        }
        {
            var Q0;
            Q0=makeQuery(id+"F74.opExtrude","CAP_FACE",FACE,{"disambiguationData":[OSD([sQuery(id+"F73.wireOp",EDGE,"E148.0"),sQuery(id+"F73.wireOp",EDGE,"E149"),sQuery(id+"F73.wireOp",EDGE,"E150"),sQuery(id+"F73.wireOp",EDGE,"E151"),sQuery(id+"F73.wireOp",EDGE,"E152")])],"isStart":false});
            var sketch = newSketch(context, id + "F76", { "sketchPlane" : qUnion([Q0])});
            skCircle(sketch, "E153.0", {"center": v(665, 345) * mm, "radius": 4 * mm});
            skSolve(sketch);
        }
        {
            var Q0;
            Q0 = qSketchRegion(id + "F76", true);
            extrude(context, id + "F77", {"entities" : qUnion([Q0]), "depth" : 5 * mm, "hasSecondDirection" : true, "secondDirectionOppositeDirection" : true, "secondDirectionDepth" : (2 + 150 + 2 + 5) * mm});
        }
        {
            var Q0;
            Q0=makeQuery(id+"F74.opExtrude","SWEPT_BODY",BODY,{"disambiguationData":[OSD([sQuery(id+"F73.wireOp",EDGE,"E148.0"),sQuery(id+"F73.wireOp",EDGE,"E149"),sQuery(id+"F73.wireOp",EDGE,"E150"),sQuery(id+"F73.wireOp",EDGE,"E151"),sQuery(id+"F73.wireOp",EDGE,"E152")])]});
            var Q1;
            Q1=makeQuery(id+"F75.opPattern","COPY",BODY,{"derivedFrom":makeQuery(id+"F74.opExtrude","SWEPT_BODY",BODY,{"disambiguationData":[OSD([sQuery(id+"F73.wireOp",EDGE,"E148.0"),sQuery(id+"F73.wireOp",EDGE,"E149"),sQuery(id+"F73.wireOp",EDGE,"E150"),sQuery(id+"F73.wireOp",EDGE,"E151"),sQuery(id+"F73.wireOp",EDGE,"E152")])]}),"instanceName":"1"});
            var Q2;
            Q2=makeQuery(id+"F77.opExtrude","SWEPT_BODY",BODY,{"disambiguationData":[OSD([sQuery(id+"F76.wireOp",EDGE,"E153.0")])]});
            var Q3;
            Q3=makeQuery(id+"F72.opExtrude","SWEPT_BODY",BODY,{"disambiguationData":[OSD([sQuery(id+"F71.wireOp",EDGE,"E146"),sQuery(id+"F71.wireOp",EDGE,"E147")])]});
            var Q4;
            Q4=qCreatedBy(id+"F47.planeOp",FACE);
            mirror(context, id + "F78", {"entities" : qUnion([Q0, Q1, Q2, Q3]), "mirrorPlane" : qUnion([Q4])});
        }
        {
            var Q0;
            Q0=makeQuery(id+"F36.opExtrude","SWEPT_FACE",FACE,{"disambiguationData":[OSD([sQuery(id+"F35.wireOp",EDGE,"E67")])]});
            var sketch = newSketch(context, id + "F79", { "sketchPlane" : qUnion([Q0])});
            skLineSegment(sketch, "E154", {"start": v(0, 154.2) * mm, "end": v(1190, 154.2) * mm, "construction": true});
            skCircle(sketch, "E155", {"center": v(196.22, 154.2) * mm, "radius": 32.5 * mm});
            skCircle(sketch, "E156", {"center": v(296.22, 154.2) * mm, "radius": 32.5 * mm});
            skCircle(sketch, "E157", {"center": v(545, 154.2) * mm, "radius": 32.5 * mm});
            skCircle(sketch, "E158", {"center": v(645, 154.2) * mm, "radius": 32.5 * mm});
            skCircle(sketch, "E159", {"center": v(908.01, 154.2) * mm, "radius": 32.5 * mm});
            skCircle(sketch, "E160", {"center": v(1008.01, 154.2) * mm, "radius": 32.5 * mm});
            skEllipse(sketch, "E161.0.0", {"center": v(246.22, 516.9) * mm, "majorRadius": 125 * mm, "minorRadius": 88.39 * mm, "majorAxis": v(1, 0), "construction": true});
            skEllipse(sketch, "E162.0.0", {"center": v(958.01, 516.9) * mm, "majorRadius": 125 * mm, "minorRadius": 88.39 * mm, "majorAxis": v(1, 0), "construction": true});
            skLineSegment(sketch, "E163", {"start": v(246.22, 516.9) * mm, "end": v(246.22, -344.74) * mm, "construction": true});
            skLineSegment(sketch, "E164", {"start": v(958.01, 516.9) * mm, "end": v(958.01, -334.74) * mm, "construction": true});
            skEllipse(sketch, "E165.0.0", {"center": v(595, 559.32) * mm, "majorRadius": 87.5 * mm, "minorRadius": 61.87 * mm, "majorAxis": v(1, 0), "construction": true});
            skLineSegment(sketch, "E166", {"start": v(595, 559.32) * mm, "end": v(595, -343.49) * mm, "construction": true});
            skSolve(sketch);
        }
        {
            var Q0;
            Q0 = qSketchRegion(id + "F79", true);
            extrude(context, id + "F80", {"entities" : qUnion([Q0]), "depth" : 25 * mm});
        }
    });
